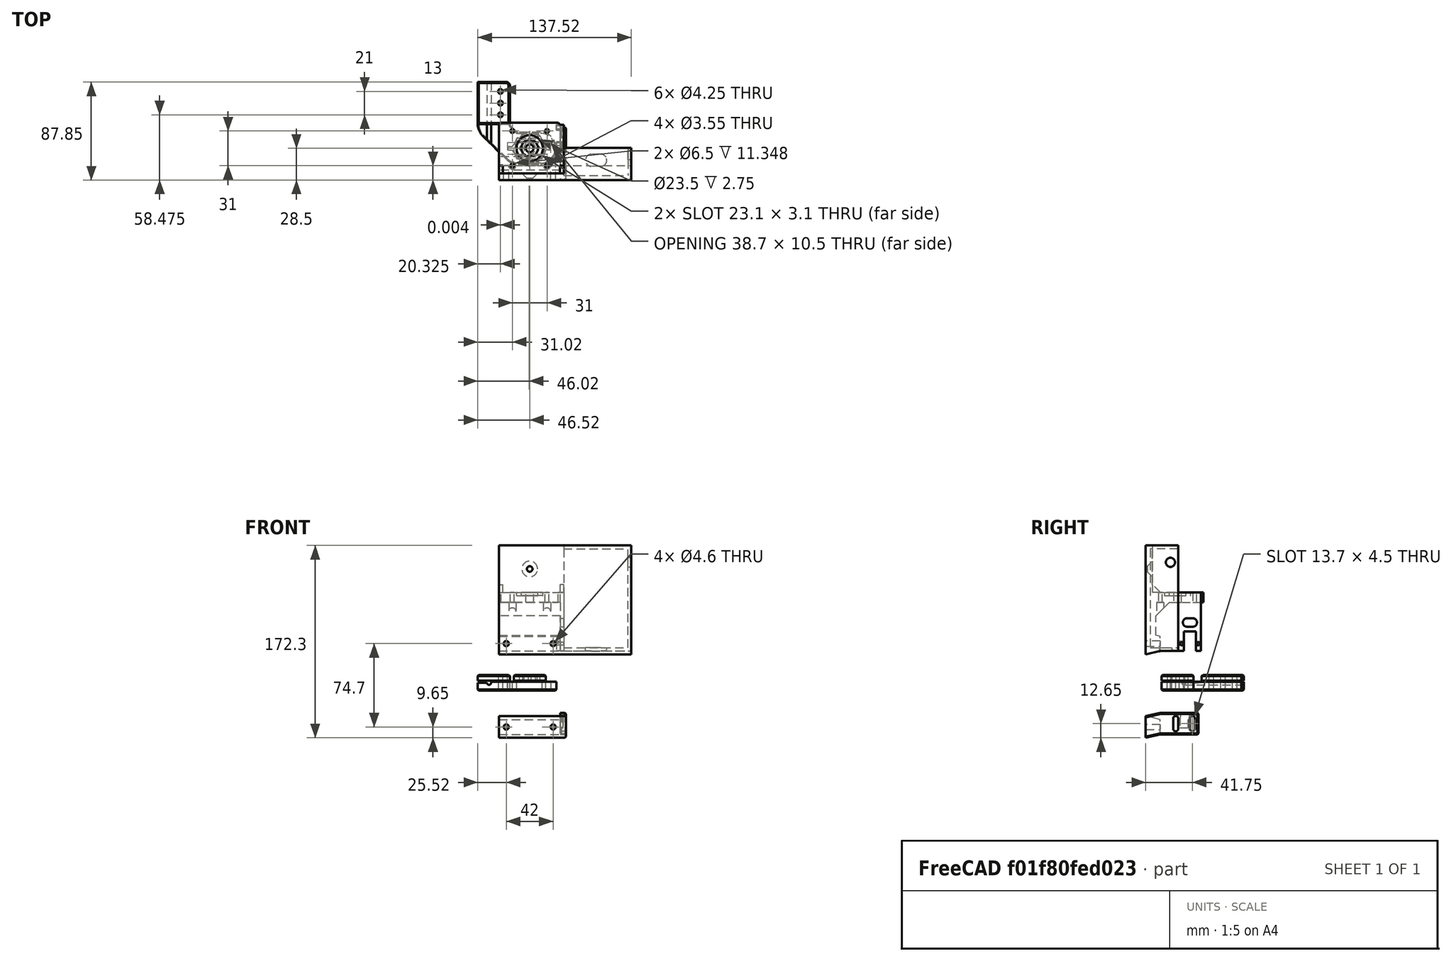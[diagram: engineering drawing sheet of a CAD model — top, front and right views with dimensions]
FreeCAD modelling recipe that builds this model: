
FCSTD DOCUMENT  (FreeCAD 1.0RUnknown)
Label: Mount_Mk2
License: All rights reserved
LicenseURL: https://en.wikipedia.org/wiki/All_rights_reserved
objects: Sketcher::SketchObject×24, PartDesign::Pad×13, PartDesign::Pocket×10, PartDesign::Chamfer×6, App::FeaturePython×6, PartDesign::Body×5, App::Link×5, Spreadsheet::Sheet×1, PartDesign::Hole×1, Assembly::JointGroup×1, Assembly::AssemblyObject×1
note: 143 computed .brp shape members not serialized (recipe doc carries the construction recipe); baked Part::Feature solids carry a one-line shape summary decoded from their .brp

FEATURE [Sketcher::SketchObject] Sketch
  ArcFitTolerance = 1e-06
  AttachmentSupport = -> [XZ_Plane]
  FullyConstrained = true
  MakeInternals = false
  MapMode = 5
  Placement = pos=(0,0,0) rot=(1,0,0;1.5708rad)
  sketch-geometry (6):
    g0: LineSegment StartX=0 StartY=0 StartZ=0 EndX=19.3 EndY=0 EndZ=0
    g1: LineSegment StartX=19.3 StartY=0 StartZ=0 EndX=16.3 EndY=13 EndZ=0
    g2: LineSegment StartX=16.3 StartY=13 StartZ=0 EndX=3 EndY=13 EndZ=0
    g3: LineSegment StartX=3 StartY=13 StartZ=0 EndX=0 EndY=0 EndZ=0
    g4: LineSegment [constr] StartX=16.3 StartY=13 StartZ=0 EndX=19.3 EndY=13 EndZ=0
    g5: LineSegment [constr] StartX=19.3 StartY=13 StartZ=0 EndX=19.3 EndY=0 EndZ=0
  constraints (16):
    c: Coincident(g-1,g0)
    c: PointOnObject(g0,g-1)
    c: Coincident(g0,g1)
    c: Coincident(g1,g2)
    c: Horizontal(g2)
    c: Coincident(g2,g3)
    c: Coincident(g3,g0)
    c: Equal(g3,g1)
    c: DistanceX(g2,g2) = 13.3
    c: Coincident(g1,g4)
    c: Horizontal(g4)
    c: Coincident(g4,g5)
    c: Coincident(g5,g0)
    c: Vertical(g5)
    c: DistanceY(g5,g5) = 13
    c: DistanceX(g4,g4) = 3
FEATURE [PartDesign::Pad] Pad
  Direction = (0,-1,2e-16)
  Length = 55
  Length2 = 10
  Placement = pos=(0,0,0) rot=(1,0,0;1.5708rad)
  Profile = -> Sketch
  ReferenceAxis = -> Sketch [N_Axis]
  Refine = true
  Suppressed = false
  Type = 0
FEATURE [Sketcher::SketchObject] Sketch001
  ArcFitTolerance = 1e-06
  AttachmentSupport = -> [Pad]
  ExternalGeometry = -> [Pad]
  FullyConstrained = true
  MakeInternals = false
  MapMode = 5
  Placement = pos=(0,5.7e-15,13) rot=(0,0,1;3.14159rad)
  sketch-geometry (5):
    g0: Circle CenterX=-9.65 CenterY=6.5 CenterZ=0 NormalX=0 NormalY=0 NormalZ=1 AngleXU=0 Radius=2.3
    g1: Circle CenterX=-9.65 CenterY=48.5 CenterZ=0 NormalX=0 NormalY=0 NormalZ=1 AngleXU=0 Radius=2.3
    g2: LineSegment [constr] StartX=-9.65 StartY=6.5 StartZ=0 EndX=-9.65 EndY=48.5 EndZ=0
    g3: LineSegment [constr] StartX=-9.65 StartY=48.5 StartZ=0 EndX=-9.65 EndY=55 EndZ=0
    g4: LineSegment [constr] StartX=-9.65 StartY=6.5 StartZ=0 EndX=-9.65 EndY=0 EndZ=0
  constraints (12):
    c: Coincident(g2,g0)
    c: Coincident(g2,g1)
    c: Vertical(g2)
    c: Coincident(g3,g1)
    c: Symmetric(g-6,g-6,g3)
    c: Vertical(g3)
    c: Coincident(g4,g0)
    c: Symmetric(g-5,g-5,g4)
    c: Equal(g0,g1)
    c: DistanceY(g2,g2) = 42
    c: Equal(g3,g4)
    c: Diameter(g1) = 4.6
FEATURE [PartDesign::Pocket] Pocket
  BaseFeature = -> Pad
  Direction = (0,0,-1)
  Length = 5
  Length2 = 5
  Placement = pos=(0,0,0) rot=(1,0,0;1.5708rad)
  Profile = -> Sketch001
  ReferenceAxis = -> Sketch001 [N_Axis]
  Refine = true
  Suppressed = false
  Type = 1
FEATURE [Sketcher::SketchObject] Sketch002
  ArcFitTolerance = 1e-06
  AttachmentSupport = -> [XZ_Plane001]
  FullyConstrained = true
  MakeInternals = false
  MapMode = 5
  Placement = pos=(0,0,0) rot=(1,0,0;1.5708rad)
  sketch-geometry (32):
    g0: LineSegment StartX=0 StartY=0 StartZ=0 EndX=97.6 EndY=0 EndZ=0
    g1: LineSegment StartX=97.6 StartY=0 StartZ=0 EndX=94.6 EndY=13 EndZ=0
    g2: LineSegment StartX=94.6 StartY=13 StartZ=0 EndX=81.3 EndY=13 EndZ=0
    g3: LineSegment StartX=81.3 StartY=13 StartZ=0 EndX=80.3769 EndY=9 EndZ=0
    g4: LineSegment StartX=80.3769 StartY=9 StartZ=0 EndX=51.1 EndY=9 EndZ=0
    g5: LineSegment StartX=51.1 StartY=9 StartZ=0 EndX=51.1 EndY=51.55 EndZ=0
    g6: LineSegment StartX=51.1 StartY=51.55 StartZ=0 EndX=42.1 EndY=51.55 EndZ=0
    g7: LineSegment StartX=42.1 StartY=51.55 StartZ=0 EndX=42.1 EndY=6 EndZ=0
    g8: LineSegment StartX=42.1 StartY=6 StartZ=0 EndX=0 EndY=6 EndZ=0
    g9: LineSegment StartX=0 StartY=6 StartZ=0 EndX=0 EndY=0 EndZ=0
    g10: LineSegment [constr] StartX=94.6 StartY=13 StartZ=0 EndX=97.6 EndY=13 EndZ=0
    g11: LineSegment [constr] StartX=97.6 StartY=13 StartZ=0 EndX=97.6 EndY=0 EndZ=0
    g12: LineSegment [constr] StartX=80.3769 StartY=9 StartZ=0 EndX=78.3 EndY=0 EndZ=0
    g13: LineSegment [constr] StartX=78.3 StartY=0 StartZ=0 EndX=78.3 EndY=13 EndZ=0
    g14: LineSegment [constr] StartX=78.3 StartY=13 StartZ=0 EndX=81.3 EndY=13 EndZ=0
    g15: LineSegment [constr] StartX=81.3 StartY=13 StartZ=0 EndX=81.3 EndY=0 EndZ=0
    g16: LineSegment [constr] StartX=3 StartY=49.55 StartZ=0 EndX=42.3 EndY=49.55 EndZ=0
    g17: LineSegment [constr] StartX=42.3 StartY=7.45 StartZ=0 EndX=3 EndY=7.45 EndZ=0
    g18: LineSegment [constr] StartX=3 StartY=7.45 StartZ=0 EndX=3 EndY=49.55 EndZ=0
    g19: LineSegment [constr] StartX=42.3 StartY=45.5 StartZ=0 EndX=59.3 EndY=45.5 EndZ=0
    g20: LineSegment [constr] StartX=59.3 StartY=45.5 StartZ=0 EndX=59.3 EndY=42.5 EndZ=0
    g21: LineSegment [constr] StartX=59.3 StartY=42.5 StartZ=0 EndX=42.3 EndY=42.5 EndZ=0
    g22: LineSegment [constr] StartX=42.3 StartY=14.5 StartZ=0 EndX=59.3 EndY=14.5 EndZ=0
    g23: LineSegment [constr] StartX=59.3 StartY=14.5 StartZ=0 EndX=59.3 EndY=11.5 EndZ=0
    g24: LineSegment [constr] StartX=59.3 StartY=11.5 StartZ=0 EndX=42.3 EndY=11.5 EndZ=0
    g25: LineSegment [constr] StartX=42.3 StartY=49.55 StartZ=0 EndX=42.3 EndY=45.5 EndZ=0
    g26: LineSegment [constr] StartX=42.3 StartY=45.5 StartZ=0 EndX=42.3 EndY=42.5 EndZ=0
    g27: LineSegment [constr] StartX=42.3 StartY=42.5 StartZ=0 EndX=42.3 EndY=14.5 EndZ=0
    g28: LineSegment [constr] StartX=42.3 StartY=14.5 StartZ=0 EndX=42.3 EndY=11.5 EndZ=0
    g29: LineSegment [constr] StartX=42.3 StartY=11.5 StartZ=0 EndX=42.3 EndY=7.45 EndZ=0
    g30: LineSegment [constr] StartX=42.3 StartY=13 StartZ=0 EndX=59.3 EndY=13 EndZ=0
    g31: LineSegment [constr] StartX=42.3 StartY=44 StartZ=0 EndX=59.3 EndY=44 EndZ=0
  constraints (89):
    c: Coincident(g-1,g0)
    c: PointOnObject(g0,g-1)
    c: Coincident(g0,g1)
    c: Coincident(g1,g2)
    c: Horizontal(g2)
    c: Coincident(g2,g3)
    c: Coincident(g3,g4)
    c: Horizontal(g4)
    c: Coincident(g4,g5)
    c: Vertical(g5)
    c: Coincident(g5,g6)
    c: Horizontal(g6)
    c: Coincident(g6,g7)
    c: Vertical(g7)
    c: Coincident(g7,g8)
    c: PointOnObject(g8,g-2)
    c: Horizontal(g8)
    c: Coincident(g8,g9)
    c: Coincident(g9,g0)
    c: Coincident(g1,g10)
    c: Horizontal(g10)
    c: Coincident(g10,g11)
    c: Coincident(g11,g0)
    c: Vertical(g11)
    c: DistanceX(g2,g2) = 13.3
    c: Coincident(g3,g12)
    c: PointOnObject(g12,g0)
    c: Coincident(g12,g13)
    c: Vertical(g13)
    c: Coincident(g13,g14)
    c: Coincident(g14,g2)
    c: Parallel(g12,g3)
    c: Horizontal(g14)
    c: Equal(g14,g10)
    c: DistanceY(g11,g11) = 13
    c: Distance(g10,g10) = 3
    c: Coincident(g2,g15)
    c: PointOnObject(g15,g0)
    c: Vertical(g15)
    c: DistanceX(g6,g6) = 9
    c: DistanceY(g9,g9) = 6
    c: Horizontal(g16)
    c: Horizontal(g17)
    c: Coincident(g17,g18)
    c: Coincident(g18,g16)
    c: Vertical(g18)
    c: Horizontal(g19)
    c: Coincident(g19,g20)
    c: Vertical(g20)
    c: Coincident(g20,g21)
    c: Horizontal(g21)
    c: Horizontal(g22)
    c: Coincident(g22,g23)
    c: Vertical(g23)
    c: Coincident(g23,g24)
    c: Horizontal(g24)
    c: Equal(g19,g22)
    c: Equal(g20,g23)
    c: Coincident(g16,g25)
    c: Coincident(g25,g19)
    c: Vertical(g25)
    c: Coincident(g25,g26)
    c: Coincident(g26,g21)
    c: Vertical(g26)
    c: Coincident(g26,g27)
    c: Coincident(g27,g22)
    c: Vertical(g27)
    c: Coincident(g27,g28)
    c: Coincident(g28,g24)
    c: Vertical(g28)
    c: Coincident(g28,g29)
    c: Coincident(g29,g17)
    c: Vertical(g29)
    c: Equal(g25,g29)
    c: Symmetric(g28,g28,g30)
    c: Symmetric(g23,g23,g30)
    c: Symmetric(g26,g26,g31)
    c: Symmetric(g20,g20,g31)
    c: Distance(g31,g30) = 31
    c: DistanceY(g18,g18) = 42.1
    c: Distance(g7,g25) = 0.2
    c: Distance(g8,g30) = 7
    c: Distance(g6,g16) = 2
    c: DistanceX(g16,g16) = 39.3
    c: Distance(g18,g9) = 3
    c: Distance(g4,g30) = 4
    c: DistanceX(g19,g19) = 17
    c: DistanceY(g20,g20) = 3
    c: Distance(g15,g27) = 39
FEATURE [PartDesign::Pad] Pad001
  Direction = (0,-1,2e-16)
  Length = 55
  Length2 = 10
  Placement = pos=(0,0,0) rot=(1,0,0;1.5708rad)
  Profile = -> Sketch002
  ReferenceAxis = -> Sketch002 [N_Axis]
  Refine = true
  Suppressed = false
  Type = 0
FEATURE [Sketcher::SketchObject] Sketch003
  ArcFitTolerance = 1e-06
  AttachmentSupport = -> [Pad001]
  ExternalGeometry = -> [Pad001]
  FullyConstrained = true
  MakeInternals = false
  MapMode = 5
  Placement = pos=(42.1,0,0) rot=(0.707107,0,-0.707107;3.14159rad)
  sketch-geometry (13):
    g0: Circle CenterX=-44 CenterY=12 CenterZ=0 NormalX=0 NormalY=0 NormalZ=1 AngleXU=0 Radius=1.775
    g1: Circle CenterX=-44 CenterY=43 CenterZ=0 NormalX=0 NormalY=0 NormalZ=1 AngleXU=0 Radius=1.775
    g2: Circle CenterX=-13 CenterY=12 CenterZ=0 NormalX=0 NormalY=0 NormalZ=1 AngleXU=0 Radius=1.775
    g3: Circle CenterX=-13 CenterY=43 CenterZ=0 NormalX=0 NormalY=0 NormalZ=1 AngleXU=0 Radius=1.775
    g4: Circle CenterX=-28.5 CenterY=27.5 CenterZ=0 NormalX=0 NormalY=0 NormalZ=1 AngleXU=0 Radius=3.5
    g5: LineSegment [constr] StartX=-44 StartY=12 StartZ=0 EndX=-44 EndY=43 EndZ=0
    g6: LineSegment [constr] StartX=-44 StartY=43 StartZ=0 EndX=-13 EndY=43 EndZ=0
    g7: LineSegment [constr] StartX=-13 StartY=43 StartZ=0 EndX=-13 EndY=12 EndZ=0
    g8: LineSegment [constr] StartX=-13 StartY=12 StartZ=0 EndX=-44 EndY=12 EndZ=0
    g9: LineSegment [constr] StartX=-44 StartY=27.5 StartZ=0 EndX=-28.5 EndY=27.5 EndZ=0
    g10: LineSegment [constr] StartX=-28.5 StartY=27.5 StartZ=0 EndX=-28.5 EndY=12 EndZ=0
    g11: LineSegment [constr] StartX=-13 StartY=12 StartZ=0 EndX=-13 EndY=-3.6e-15 EndZ=0
    g12: LineSegment [constr] StartX=-13 StartY=43 StartZ=0 EndX=-13 EndY=55 EndZ=0
  constraints (33):
    c: Coincident(g5,g0)
    c: Coincident(g5,g1)
    c: Vertical(g5)
    c: Coincident(g5,g6)
    c: Coincident(g6,g3)
    c: Horizontal(g6)
    c: Coincident(g6,g7)
    c: Coincident(g7,g2)
    c: Vertical(g7)
    c: Coincident(g7,g8)
    c: Coincident(g8,g5)
    c: Horizontal(g8)
    c: Symmetric(g5,g5,g9)
    c: Coincident(g9,g4)
    c: Horizontal(g9)
    c: Coincident(g9,g10)
    c: Symmetric(g8,g8,g10)
    c: Vertical(g10)
    c: Equal(g6,g5)
    c: DistanceX(g6,g6) = 31
    c: Distance(g-5,g7) = 7
    c: Coincident(g11,g2)
    c: PointOnObject(g11,g-6)
    c: Vertical(g11)
    c: Coincident(g12,g3)
    c: Vertical(g12)
    c: Equal(g11,g12)
    c: Equal(g1,g0)
    c: Equal(g0,g3)
    c: Equal(g3,g2)
    c: Diameter(g1) = 3.55
    c: Diameter(g4) = 7
    c: PointOnObject(g12,g-3)
FEATURE [PartDesign::Pocket] Pocket001
  BaseFeature = -> Pad001
  Direction = (1,0,2e-16)
  Length = 0
  Length2 = 5
  Placement = pos=(0,0,0) rot=(1,0,0;1.5708rad)
  Profile = -> Sketch003
  ReferenceAxis = -> Sketch003 [N_Axis]
  Refine = true
  Suppressed = false
  Type = 3
  UpToFace = -> Pad001 [Face6]
FEATURE [Sketcher::SketchObject] Sketch004
  ArcFitTolerance = 1e-06
  AttachmentSupport = -> [Pocket001]
  ExternalGeometry = -> [Pocket001]
  FullyConstrained = true
  MakeInternals = false
  MapMode = 5
  Placement = pos=(42.1,0,0) rot=(0.707107,0,-0.707107;3.14159rad)
  sketch-geometry (2):
    g0: Circle CenterX=-28.5 CenterY=27.5 CenterZ=0 NormalX=0 NormalY=0 NormalZ=1 AngleXU=0 Radius=11.75
    g1: Circle CenterX=-28.5 CenterY=27.5 CenterZ=0 NormalX=0 NormalY=0 NormalZ=1 AngleXU=0 Radius=7.5
  constraints (4):
    c: Coincident(g0,g-3)
    c: Diameter(g0) = 23.5
    c: Coincident(g1,g0)
    c: Diameter(g1) = 15
FEATURE [PartDesign::Pocket] Pocket002
  BaseFeature = -> Pocket001
  Direction = (1,0,2e-16)
  Length = 2.75
  Length2 = 5
  Placement = pos=(0,0,0) rot=(1,0,0;1.5708rad)
  Profile = -> Sketch004
  ReferenceAxis = -> Sketch004 [N_Axis]
  Refine = true
  Suppressed = false
  Type = 0
FEATURE [Sketcher::SketchObject] Sketch005
  ArcFitTolerance = 1e-06
  AttachmentSupport = -> [Pocket002]
  ExternalGeometry = -> [Pocket002]
  FullyConstrained = true
  MakeInternals = false
  MapMode = 5
  Placement = pos=(0,5.7e-15,13) rot=(0,0,1;3.14159rad)
  sketch-geometry (5):
    g0: Circle CenterX=-87.95 CenterY=48.5 CenterZ=0 NormalX=0 NormalY=0 NormalZ=1 AngleXU=0 Radius=2.3
    g1: Circle CenterX=-87.95 CenterY=6.5 CenterZ=0 NormalX=0 NormalY=0 NormalZ=1 AngleXU=0 Radius=2.3
    g2: LineSegment [constr] StartX=-87.95 StartY=48.5 StartZ=0 EndX=-87.95 EndY=6.5 EndZ=0
    g3: LineSegment [constr] StartX=-87.95 StartY=48.5 StartZ=0 EndX=-87.95 EndY=55 EndZ=0
    g4: LineSegment [constr] StartX=-87.95 StartY=6.5 StartZ=0 EndX=-87.95 EndY=0 EndZ=0
  constraints (12):
    c: Coincident(g2,g0)
    c: Coincident(g2,g1)
    c: Vertical(g2)
    c: Coincident(g3,g0)
    c: Symmetric(g-3,g-3,g3)
    c: Coincident(g4,g1)
    c: Symmetric(g-6,g-6,g4)
    c: Vertical(g4)
    c: Equal(g3,g4)
    c: DistanceY(g2,g2) = 42
    c: Diameter(g0) = 4.6
    c: Equal(g0,g1)
FEATURE [PartDesign::Pocket] Pocket003
  BaseFeature = -> Pocket002
  Direction = (0,0,-1)
  Length = 5
  Length2 = 5
  Placement = pos=(0,0,0) rot=(1,0,0;1.5708rad)
  Profile = -> Sketch005
  ReferenceAxis = -> Sketch005 [N_Axis]
  Refine = true
  Suppressed = false
  Type = 1
FEATURE [PartDesign::Chamfer] Chamfer
  Angle = 45
  Base = -> Pocket003 [Edge15,Edge23]
  BaseFeature = -> Pocket003
  ChamferType = 0
  FlipDirection = false
  Placement = pos=(0,0,0) rot=(1,0,0;1.5708rad)
  Refine = true
  Size = 2
  Size2 = 1
  SupportTransform = false
  Suppressed = false
  UseAllEdges = false
FEATURE [Sketcher::SketchObject] Sketch006
  ArcFitTolerance = 1e-06
  AttachmentSupport = -> [Chamfer]
  ExternalGeometry = -> [Chamfer]
  FullyConstrained = true
  MakeInternals = false
  MapMode = 5
  Placement = pos=(0,2.6e-15,6) rot=(0,0,1;3.14159rad)
  sketch-geometry (3):
    g0: Circle CenterX=-21.05 CenterY=27.5 CenterZ=0 NormalX=0 NormalY=0 NormalZ=1 AngleXU=0 Radius=2.5
    g1: LineSegment [constr] StartX=-21.05 StartY=27.5 StartZ=0 EndX=0 EndY=27.5 EndZ=0
    g2: LineSegment [constr] StartX=-21.05 StartY=27.5 StartZ=0 EndX=-21.05 EndY=55 EndZ=0
  constraints (7):
    c: Coincident(g1,g0)
    c: Symmetric(g-4,g-4,g1)
    c: Horizontal(g1)
    c: Coincident(g2,g0)
    c: Symmetric(g-3,g-3,g2)
    c: Vertical(g2)
    c: Diameter(g0) = 5
FEATURE [PartDesign::Pocket] Pocket004
  BaseFeature = -> Chamfer
  Direction = (0,0,-1)
  Length = 5
  Length2 = 5
  Placement = pos=(0,0,0) rot=(1,0,0;1.5708rad)
  Profile = -> Sketch006
  ReferenceAxis = -> Sketch006 [N_Axis]
  Refine = true
  Suppressed = false
  Type = 1
FEATURE [PartDesign::Chamfer] Chamfer001
  Angle = 45
  Base = -> Pocket004 [Edge38]
  BaseFeature = -> Pocket004
  ChamferType = 0
  FlipDirection = false
  Placement = pos=(0,0,0) rot=(1,0,0;1.5708rad)
  Refine = true
  Size = 4.5
  Size2 = 1
  SupportTransform = false
  Suppressed = false
  UseAllEdges = false
FEATURE [Sketcher::SketchObject] Sketch007
  ArcFitTolerance = 1e-06
  AttachmentSupport = -> [XY_Plane002]
  FullyConstrained = true
  MakeInternals = false
  MapMode = 5
  expr: Constraints[122] = 3.9 + 0.35
  expr: Constraints[72] = (2.9 + 0.2) / 2
  expr: Constraints[73] = (10 + 0.5) / 2
  sketch-geometry (53):
    g0: ArcOfCircle CenterX=0 CenterY=0 CenterZ=0 NormalX=0 NormalY=0 NormalZ=1 AngleXU=0 Radius=14.35 StartAngle=4.71239 EndAngle=7.85398
    g1: ArcOfCircle CenterX=-20 CenterY=9e-16 CenterZ=0 NormalX=0 NormalY=0 NormalZ=1 AngleXU=0 Radius=14.35 StartAngle=3.92699 EndAngle=4.71239
    g2: ArcOfCircle CenterX=-41.666 CenterY=21.666 CenterZ=0 NormalX=0 NormalY=0 NormalZ=1 AngleXU=0 Radius=14.35 StartAngle=3.14159 EndAngle=3.92699
    g3: ArcOfCircle CenterX=0 CenterY=7.8 CenterZ=0 NormalX=0 NormalY=0 NormalZ=1 AngleXU=0 Radius=1.55 StartAngle=4.71239 EndAngle=7.85398
    g4: ArcOfCircle CenterX=-20 CenterY=7.8 CenterZ=0 NormalX=0 NormalY=0 NormalZ=1 AngleXU=0 Radius=1.55 StartAngle=1.5708 EndAngle=4.71239
    g5: ArcOfCircle CenterX=-20 CenterY=-7.8 CenterZ=0 NormalX=0 NormalY=0 NormalZ=1 AngleXU=0 Radius=1.55 StartAngle=1.5708 EndAngle=4.71239
    g6: ArcOfCircle CenterX=0 CenterY=-7.8 CenterZ=0 NormalX=0 NormalY=0 NormalZ=1 AngleXU=0 Radius=1.55 StartAngle=4.71239 EndAngle=7.85398
    g7: ArcOfCircle CenterX=7.8 CenterY=-3e-16 CenterZ=0 NormalX=0 NormalY=0 NormalZ=1 AngleXU=0 Radius=1.55 StartAngle=4.71239 EndAngle=7.85398
    g8: ArcOfCircle CenterX=-27.8 CenterY=1.7e-15 CenterZ=0 NormalX=0 NormalY=0 NormalZ=1 AngleXU=0 Radius=1.55 StartAngle=1.5708 EndAngle=4.71239
    g9: LineSegment StartX=-20 StartY=9.35 StartZ=0 EndX=0 EndY=9.35 EndZ=0
    g10: LineSegment StartX=-20 StartY=6.25 StartZ=0 EndX=0 EndY=6.25 EndZ=0
    g11: LineSegment StartX=-20 StartY=5.25 StartZ=0 EndX=0 EndY=5.25 EndZ=0
    g12: LineSegment StartX=-20 StartY=-5.25 StartZ=0 EndX=0 EndY=-5.25 EndZ=0
    g13: LineSegment StartX=-20 StartY=-6.25 StartZ=0 EndX=0 EndY=-6.25 EndZ=0
    g14: LineSegment StartX=-20 StartY=-9.35 StartZ=0 EndX=0 EndY=-9.35 EndZ=0
    g15: LineSegment StartX=-20 StartY=-14.35 StartZ=0 EndX=-3.6e-15 EndY=-14.35 EndZ=0
    g16: LineSegment StartX=-27.8 StartY=1.55 StartZ=0 EndX=-25.016 EndY=1.55 EndZ=0
    g17: LineSegment StartX=-27.8 StartY=-1.55 StartZ=0 EndX=-25.016 EndY=-1.55 EndZ=0
    g18: LineSegment StartX=5.01597 StartY=1.55 StartZ=0 EndX=7.8 EndY=1.55 EndZ=0
    g19: LineSegment StartX=7.8 StartY=-1.55 StartZ=0 EndX=5.01597 EndY=-1.55 EndZ=0
    g20: LineSegment StartX=4.4e-15 StartY=14.35 StartZ=0 EndX=-20 EndY=14.35 EndZ=0
    g21: LineSegment StartX=-51.813 StartY=11.519 StartZ=0 EndX=-30.147 EndY=-10.147 EndZ=0
    g22: LineSegment StartX=-56.016 StartY=21.666 StartZ=0 EndX=-56.016 EndY=59.35 EndZ=0
    g23: LineSegment [constr] StartX=-20 StartY=-1e-16 StartZ=0 EndX=-20 EndY=7.8 EndZ=0
    g24: LineSegment [constr] StartX=-20 StartY=-7.8 StartZ=0 EndX=-20 EndY=0 EndZ=0
    g25: LineSegment [constr] StartX=0 StartY=-7.8 StartZ=0 EndX=0 EndY=0 EndZ=0
    g26: LineSegment [constr] StartX=0 StartY=0 StartZ=0 EndX=0 EndY=7.8 EndZ=0
    g27: LineSegment [constr] StartX=0 StartY=0 StartZ=0 EndX=7.8 EndY=-3e-16 EndZ=0
    g28: LineSegment [constr] StartX=-27.8 StartY=1.7e-15 StartZ=0 EndX=-20 EndY=-1e-16 EndZ=0
    g29: ArcOfCircle CenterX=0 CenterY=0 CenterZ=0 NormalX=0 NormalY=0 NormalZ=1 AngleXU=0 Radius=5.25 StartAngle=0.299705 EndAngle=1.5708
    g30: ArcOfCircle CenterX=0 CenterY=0 CenterZ=0 NormalX=0 NormalY=0 NormalZ=1 AngleXU=0 Radius=5.25 StartAngle=4.71239 EndAngle=5.98348
    g31: ArcOfCircle CenterX=-20 CenterY=-1e-16 CenterZ=0 NormalX=0 NormalY=0 NormalZ=1 AngleXU=0 Radius=5.25 StartAngle=1.5708 EndAngle=2.84189
    g32: ArcOfCircle CenterX=-20 CenterY=-1e-16 CenterZ=0 NormalX=0 NormalY=0 NormalZ=1 AngleXU=0 Radius=5.25 StartAngle=3.4413 EndAngle=4.71239
    g33: LineSegment StartX=-21.4142 StartY=14.9358 StartZ=0 EndX=-26.7302 EndY=20.2518 EndZ=0
    g34: LineSegment StartX=-27.316 StartY=21.666 StartZ=0 EndX=-27.316 EndY=57.2287 EndZ=0
    g35: ArcOfCircle CenterX=-25.316 CenterY=21.666 CenterZ=0 NormalX=0 NormalY=0 NormalZ=1 AngleXU=0 Radius=2 StartAngle=3.14159 EndAngle=3.92699
    g36: ArcOfCircle CenterX=-20 CenterY=16.35 CenterZ=0 NormalX=0 NormalY=0 NormalZ=1 AngleXU=0 Radius=2 StartAngle=3.92699 EndAngle=4.71239
    g37: LineSegment StartX=-27.316 StartY=57.2287 StartZ=0 EndX=-29.4373 EndY=59.35 EndZ=0
    g38: LineSegment StartX=-56.016 StartY=59.35 StartZ=0 EndX=-29.4373 EndY=59.35 EndZ=0
    g39: LineSegment [constr] StartX=-20 StartY=-14.35 StartZ=0 EndX=-56.016 EndY=-14.35 EndZ=0
    g40: LineSegment [constr] StartX=-56.016 StartY=-14.35 StartZ=0 EndX=-56.016 EndY=21.666 EndZ=0
    g41: LineSegment [constr] StartX=-47.766 StartY=59.35 StartZ=0 EndX=-47.766 EndY=-14.35 EndZ=0
    g42: LineSegment [constr] StartX=-44.016 StartY=59.35 StartZ=0 EndX=-44.016 EndY=-14.35 EndZ=0
    g43: Circle CenterX=-35.691 CenterY=50.975 CenterZ=0 NormalX=0 NormalY=0 NormalZ=1 AngleXU=0 Radius=2.125
    g44: Circle CenterX=-35.691 CenterY=40.475 CenterZ=0 NormalX=0 NormalY=0 NormalZ=1 AngleXU=0 Radius=2.125
    g45: Circle CenterX=-35.691 CenterY=29.975 CenterZ=0 NormalX=0 NormalY=0 NormalZ=1 AngleXU=0 Radius=2.125
    g46: LineSegment [constr] StartX=-35.691 StartY=53.1 StartZ=0 EndX=-35.691 EndY=59.35 EndZ=0
    g47: LineSegment [constr] StartX=-35.691 StartY=48.85 StartZ=0 EndX=-35.691 EndY=42.6 EndZ=0
    g48: LineSegment [constr] StartX=-35.691 StartY=38.35 StartZ=0 EndX=-35.691 EndY=32.1 EndZ=0
    g49: LineSegment [constr] StartX=-56.016 StartY=21.666 StartZ=0 EndX=-27.316 EndY=21.666 EndZ=0
    g50: LineSegment [constr] StartX=-33.566 StartY=50.975 StartZ=0 EndX=-27.316 EndY=50.975 EndZ=0
    g51: LineSegment [constr] StartX=-20 StartY=7.8 StartZ=0 EndX=-20 EndY=14.35 EndZ=0
    g52: LineSegment [constr] StartX=-20 StartY=-7.8 StartZ=0 EndX=-20 EndY=-14.35 EndZ=0
  constraints (142):
    c: Horizontal(g9)
    c: Horizontal(g10)
    c: Horizontal(g11)
    c: Horizontal(g12)
    c: Horizontal(g13)
    c: Horizontal(g14)
    c: Horizontal(g15)
    c: Tangent(g9,g4) = 1.5708
    c: Tangent(g10,g4) = -1.5708
    c: Tangent(g10,g3) = -1.5708
    c: Tangent(g9,g3) = 1.5708
    c: Tangent(g13,g6) = 1.5708
    c: Tangent(g14,g6) = -1.5708
    c: Tangent(g13,g5) = 1.5708
    c: Tangent(g14,g5) = -1.5708
    c: Horizontal(g16)
    c: Horizontal(g18)
    c: Horizontal(g19)
    c: Horizontal(g17)
    c: Tangent(g16,g8) = 1.5708
    c: Tangent(g17,g8) = -1.5708
    c: Equal(g16,g17)
    c: Tangent(g18,g7) = 1.5708
    c: Tangent(g19,g7) = 1.5708
    c: Equal(g18,g19)
    c: Horizontal(g20)
    c: Tangent(g21,g1) = -1.5708
    c: Tangent(g21,g2) = -1.5708
    c: Angle(g15,g21) = 2.35619
    c: Vertical(g22)
    c: Tangent(g22,g2) = 1.5708
    c: Tangent(g15,g0) = -1.5708
    c: Tangent(g20,g0) = -1.5708
    c: Tangent(g15,g1) = -1.5708
    c: Coincident(g0,g-1)
    c: Coincident(g23,g4)
    c: Vertical(g23)
    c: Coincident(g24,g5)
    c: Coincident(g25,g6)
    c: Coincident(g25,g0)
    c: Coincident(g26,g0)
    c: Coincident(g26,g3)
    c: Vertical(g24)
    c: Vertical(g25)
    c: Vertical(g26)
    c: Equal(g23,g24)
    c: Coincident(g27,g0)
    c: Coincident(g27,g7)
    c: Coincident(g28,g8)
    c: Coincident(g29,g0)
    c: Coincident(g29,g18)
    c: Coincident(g30,g0)
    c: Coincident(g30,g19)
    c: Coincident(g31,g23)
    c: Coincident(g31,g16)
    c: Coincident(g32,g24)
    c: Coincident(g32,g17)
    c: Equal(g30,g29)
    c: Equal(g29,g32)
    c: Coincident(g24,g23)
    c: Coincident(g24,g28)
    c: Equal(g27,g26)
    c: Equal(g23,g28)
    c: Equal(g8,g4)
    c: Equal(g5,g4)
    c: Tangent(g31,g11) = 1.5708
    c: Tangent(g32,g12) = -1.5708
    c: Tangent(g29,g11) = 1.5708
    c: Tangent(g30,g12) = -1.5708
    c: Equal(g7,g8)
    c: DistanceX(g11,g11) = 20
    c: DistanceY(g26,g26) = 7.8
    c: Radius(g3) = 1.55
    c: Radius(g31) = 5.25
    c: Distance(g20,g9) = 5
    c: Vertical(g34)
    c: Equal(g35,g36)
    c: Equal(g2,g1)
    c: Equal(g1,g0)
    c: Radius(g36) = 2
    c: Tangent(g36,g20) = 1.5708
    c: Tangent(g36,g33) = 1.5708
    c: Tangent(g35,g33) = 1.5708
    c: Tangent(g35,g34) = 1.5708
    c: Parallel(g21,g33)
    c: Coincident(g37,g34)
    c: Coincident(g38,g22)
    c: Coincident(g38,g37)
    c: Horizontal(g38)
    c: Angle(g38,g37) = 2.35619
    c: Distance(g37,g37) = 3
    c: Tangent(g39,g1) = 1.5708
    c: Vertical(g40)
    c: Coincident(g2,g40)
    c: Coincident(g40,g39)
    c: PointOnObject(g41,g38)
    c: PointOnObject(g41,g39)
    c: Vertical(g41)
    c: PointOnObject(g42,g38)
    c: PointOnObject(g42,g39)
    c: Vertical(g42)
    c: Distance(g42,g22) = 12
    c: Distance(g42,g41) = 3.75
    c: Distance(g16,g42) = 19
    c: Distance(g20,g38) = 45
    c: Equal(g43,g44)
    c: Equal(g44,g45)
    c: PointOnObject(g46,g43)
    c: PointOnObject(g46,g38)
    c: Vertical(g46)
    c: PointOnObject(g47,g43)
    c: PointOnObject(g47,g44)
    c: Vertical(g47)
    c: PointOnObject(g48,g44)
    c: PointOnObject(g48,g45)
    c: Vertical(g48)
    c: Perpendicular(g43,g46)
    c: Perpendicular(g43,g47)
    c: Perpendicular(g44,g47)
    c: Perpendicular(g44,g48)
    c: Perpendicular(g45,g48)
    c: Equal(g47,g48)
    c: Diameter(g45) = 4.25
    c: Coincident(g49,g2)
    c: Coincident(g49,g34)
    c: Horizontal(g49)
    c: PointOnObject(g50,g43)
    c: PointOnObject(g50,g34)
    c: Horizontal(g50)
    c: Perpendicular(g43,g50)
    c: DistanceX(g50,g50) = 6.25
    c: Coincident(g51,g4)
    c: Coincident(g51,g20)
    c: Coincident(g52,g5)
    c: Coincident(g52,g1)
    c: Vertical(g52)
    c: Vertical(g51)
    c: Equal(g46,g47)
    c: Equal(g50,g46)
    c: Distance(g34,g22) = 28.7
    c: DistanceY(g22,g22) = 37.684
    c: Distance(g0,g38) = 59.35
FEATURE [Spreadsheet::Sheet] Spreadsheet  label="Params"
  cells = A2='M3 Shaft Diameter; B2==2.9 mm; A3='M4 Shaft Diameter; B3==3.9 mm; A4='Bolt Tolerance; B4==0.2 mm; A6='Part Thickness; B6==8 mm; A8='Main Slot Length; B8==20 mm; A9='Main Slot Diameter; B9==10 mm; A10='Main Slot Tolerance; B10==0.5 mm; A11='Object Diameter; B11==28 mm; A13='Window Grab Diameter; B13==3.75 mm; A14='Window Grab Length; B14==12 mm; A15='Window Grab Thickness; B15==2 mm
FEATURE [PartDesign::Pad] Pad002
  Direction = (0,0,1)
  Length = 8
  Length2 = 10
  Profile = -> Sketch007
  ReferenceAxis = -> Sketch007 [N_Axis]
  Refine = true
  Suppressed = false
  Type = 0
FEATURE [Sketcher::SketchObject] Sketch008
  ArcFitTolerance = 1e-06
  AttachmentSupport = -> [Pad002]
  ExternalGeometry = -> [Pad002]
  FullyConstrained = true
  MakeInternals = false
  MapMode = 5
  Placement = pos=(0,59.35,0) rot=(0,0.707107,0.707107;3.14159rad)
  expr: Constraints[12] = 3.75 / 2
  sketch-geometry (5):
    g0: LineSegment StartX=56.016 StartY=7 StartZ=0 EndX=47.766 EndY=7 EndZ=0
    g1: LineSegment StartX=44.016 StartY=8 StartZ=0 EndX=44.016 EndY=7 EndZ=0
    g2: ArcOfCircle CenterX=45.891 CenterY=7 CenterZ=0 NormalX=0 NormalY=0 NormalZ=1 AngleXU=0 Radius=1.875 StartAngle=3.14159 EndAngle=6.28319
    g3: LineSegment StartX=44.016 StartY=8 StartZ=0 EndX=56.016 EndY=8 EndZ=0
    g4: LineSegment StartX=56.016 StartY=8 StartZ=0 EndX=56.016 EndY=7 EndZ=0
  constraints (14):
    c: PointOnObject(g0,g-4)
    c: Horizontal(g0)
    c: PointOnObject(g1,g-3)
    c: Vertical(g1)
    c: Coincident(g2,g0)
    c: Tangent(g2,g1) = -1.5708
    c: Perpendicular(g2,g0)
    c: Coincident(g3,g1)
    c: Coincident(g3,g-4)
    c: Coincident(g4,g3)
    c: Coincident(g4,g0)
    c: DistanceX(g3,g3) = 12
    c: Radius(g2) = 1.875
    c: DistanceY(g4,g4) = 1
FEATURE [PartDesign::Pocket] Pocket005
  BaseFeature = -> Pad002
  Direction = (0,-1,2e-16)
  Length = 5
  Length2 = 5
  Profile = -> Sketch008
  ReferenceAxis = -> Sketch008 [N_Axis]
  Refine = true
  Suppressed = false
  Type = 1
FEATURE [Sketcher::SketchObject] Sketch009
  ArcFitTolerance = 1e-06
  AttachmentSupport = -> [XY_Plane003]
  FullyConstrained = true
  MakeInternals = false
  MapMode = 5
  expr: Constraints[16] = 3.9 + 0.35
  sketch-geometry (12):
    g0: LineSegment StartX=0 StartY=-2.12132 StartZ=0 EndX=-2.12132 EndY=0 EndZ=0
    g1: LineSegment StartX=-2.12132 StartY=0 StartZ=0 EndX=-28.7 EndY=0 EndZ=0
    g2: LineSegment StartX=-28.7 StartY=0 StartZ=0 EndX=-28.7 EndY=-37.684 EndZ=0
    g3: LineSegment StartX=-28.7 StartY=-37.684 StartZ=0 EndX=0 EndY=-37.684 EndZ=0
    g4: LineSegment StartX=0 StartY=-37.684 StartZ=0 EndX=0 EndY=-2.12132 EndZ=0
    g5: Circle CenterX=-8.375 CenterY=-8.375 CenterZ=0 NormalX=0 NormalY=0 NormalZ=1 AngleXU=0 Radius=2.125
    g6: Circle CenterX=-8.375 CenterY=-18.875 CenterZ=0 NormalX=0 NormalY=0 NormalZ=1 AngleXU=0 Radius=2.125
    g7: Circle CenterX=-8.375 CenterY=-29.375 CenterZ=0 NormalX=0 NormalY=0 NormalZ=1 AngleXU=0 Radius=2.125
    g8: LineSegment [constr] StartX=-8.375 StartY=0 StartZ=0 EndX=-8.375 EndY=-6.25 EndZ=0
    g9: LineSegment [constr] StartX=-6.25 StartY=-8.375 StartZ=0 EndX=0 EndY=-8.375 EndZ=0
    g10: LineSegment [constr] StartX=-8.375 StartY=-16.75 StartZ=0 EndX=-8.375 EndY=-10.5 EndZ=0
    g11: LineSegment [constr] StartX=-8.375 StartY=-27.25 StartZ=0 EndX=-8.375 EndY=-21 EndZ=0
  constraints (40):
    c: PointOnObject(g0,g-2)
    c: PointOnObject(g0,g-1)
    c: Coincident(g0,g1)
    c: PointOnObject(g1,g-1)
    c: Coincident(g1,g2)
    c: Vertical(g2)
    c: Coincident(g2,g3)
    c: PointOnObject(g3,g-2)
    c: Horizontal(g3)
    c: Coincident(g3,g4)
    c: Coincident(g4,g0)
    c: Distance(g0,g0) = 3
    c: Angle(g1,g0) = 2.35619
    c: DistanceY(g2,g2) = 37.684
    c: Equal(g6,g5)
    c: Equal(g5,g7)
    c: Diameter(g7) = 4.25
    c: PointOnObject(g8,g1)
    c: PointOnObject(g8,g5)
    c: Vertical(g8)
    c: PointOnObject(g9,g5)
    c: PointOnObject(g9,g4)
    c: PointOnObject(g10,g6)
    c: PointOnObject(g10,g5)
    c: Vertical(g10)
    c: PointOnObject(g11,g7)
    c: PointOnObject(g11,g6)
    c: Vertical(g11)
    c: Horizontal(g9)
    c: Perpendicular(g5,g8)
    c: Perpendicular(g5,g9)
    c: Perpendicular(g5,g10)
    c: Perpendicular(g6,g10)
    c: Perpendicular(g6,g11)
    c: Perpendicular(g7,g11)
    c: Equal(g9,g8)
    c: Equal(g8,g10)
    c: Equal(g10,g11)
    c: DistanceX(g9,g9) = 6.25
    c: Distance(g4,g2) = 28.7
FEATURE [PartDesign::Pad] Pad003
  Direction = (0,0,1)
  Length = 5
  Length2 = 10
  Profile = -> Sketch009
  ReferenceAxis = -> Sketch009 [N_Axis]
  Refine = true
  Suppressed = false
  Type = 0
FEATURE [Sketcher::SketchObject] Sketch010
  ArcFitTolerance = 1e-06
  AttachmentSupport = -> [XY_Plane004]
  FullyConstrained = true
  MakeInternals = false
  MapMode = 5
  expr: Constraints[20] = 10 + 0.5
  sketch-geometry (11):
    g0: Circle CenterX=0 CenterY=0 CenterZ=0 NormalX=0 NormalY=0 NormalZ=1 AngleXU=0 Radius=14.35
    g1: Circle CenterX=0 CenterY=0 CenterZ=0 NormalX=0 NormalY=0 NormalZ=1 AngleXU=0 Radius=5.25
    g2: Circle CenterX=0 CenterY=7.8 CenterZ=0 NormalX=0 NormalY=0 NormalZ=1 AngleXU=0 Radius=1.5
    g3: Circle CenterX=7.8 CenterY=0 CenterZ=0 NormalX=0 NormalY=0 NormalZ=1 AngleXU=0 Radius=1.5
    g4: Circle CenterX=-7.8 CenterY=0 CenterZ=0 NormalX=0 NormalY=0 NormalZ=1 AngleXU=0 Radius=1.5
    g5: Circle CenterX=0 CenterY=-7.8 CenterZ=0 NormalX=0 NormalY=0 NormalZ=1 AngleXU=0 Radius=1.5
    g6: LineSegment [constr] StartX=0 StartY=0 StartZ=0 EndX=0 EndY=7.8 EndZ=0
    g7: LineSegment [constr] StartX=0 StartY=0 StartZ=0 EndX=-7.8 EndY=0 EndZ=0
    g8: LineSegment [constr] StartX=0 StartY=0 StartZ=0 EndX=0 EndY=-7.8 EndZ=0
    g9: LineSegment [constr] StartX=0 StartY=0 StartZ=0 EndX=7.8 EndY=0 EndZ=0
    g10: LineSegment [constr] StartX=0 StartY=7.8 StartZ=0 EndX=0 EndY=14.35 EndZ=0
  constraints (27):
    c: Coincident(g0,g-1)
    c: Coincident(g1,g0)
    c: PointOnObject(g2,g-2)
    c: PointOnObject(g3,g-1)
    c: PointOnObject(g4,g-1)
    c: PointOnObject(g5,g-2)
    c: Coincident(g6,g0)
    c: Coincident(g6,g2)
    c: Coincident(g7,g0)
    c: Coincident(g7,g4)
    c: Coincident(g8,g0)
    c: Coincident(g8,g5)
    c: Coincident(g9,g0)
    c: Coincident(g9,g3)
    c: Equal(g6,g7)
    c: Equal(g7,g9)
    c: Equal(g9,g8)
    c: Equal(g2,g4)
    c: Equal(g4,g5)
    c: Equal(g5,g3)
    c: Diameter(g1) = 10.5
    c: Diameter(g3) = 3
    c: DistanceY(g6,g6) = 7.8
    c: Coincident(g10,g2)
    c: PointOnObject(g10,g0)
    c: Vertical(g10)
    c: DistanceY(g10,g10) = 6.55
FEATURE [PartDesign::Pad] Pad004
  Direction = (0,0,1)
  Length = 5
  Length2 = 10
  Profile = -> Sketch010
  ReferenceAxis = -> Sketch010 [N_Axis]
  Refine = true
  Suppressed = false
  Type = 0
FEATURE [PartDesign::Chamfer] Chamfer002
  Angle = 45
  Base = -> Pad004 [Edge3]
  BaseFeature = -> Pad004
  ChamferType = 0
  FlipDirection = false
  Refine = true
  Size = 1
  Size2 = 1
  SupportTransform = false
  Suppressed = false
  UseAllEdges = false
FEATURE [PartDesign::Body] Body004  label="Window_Grab_Arm_Clamp"
  AllowCompound = false
  Group = -> [Sketch010,Pad004,Chamfer002]
  Origin = -> Origin004
  Placement = pos=(1.5,3.5,9) rot=(0,0,1;0rad)
  Tip = -> Chamfer002
FEATURE [PartDesign::Chamfer] Chamfer003
  Angle = 45
  Base = -> Pocket005 [Edge15,Edge16,Edge1,Edge5,Edge6,Edge7,Edge8,Edge9,Edge10,Edge11,Edge12,Edge13,Edge14]
  BaseFeature = -> Pocket005
  ChamferType = 0
  FlipDirection = false
  Refine = true
  Size = 1
  Size2 = 1
  SupportTransform = false
  Suppressed = false
  UseAllEdges = false
FEATURE [PartDesign::Body] Body002  label="Window_Grab_Arm"
  AllowCompound = false
  Group = -> [Sketch007,Pad002,Sketch008,Pocket005,Chamfer003]
  Origin = -> Origin002
  Placement = pos=(11,3.5,0) rot=(0,0,1;0rad)
  Tip = -> Chamfer003
FEATURE [PartDesign::Chamfer] Chamfer004
  Angle = 45
  Base = -> Pad003 [Edge10,Edge7,Edge4,Edge15,Edge13]
  BaseFeature = -> Pad003
  ChamferType = 0
  FlipDirection = false
  Refine = true
  Size = 1
  Size2 = 1
  SupportTransform = false
  Suppressed = false
  UseAllEdges = false
FEATURE [PartDesign::Body] Body003  label="Window_Grab_Clamp"
  AllowCompound = false
  Group = -> [Sketch009,Pad003,Chamfer004]
  Origin = -> Origin003
  Placement = pos=(-16.32,62.85,9) rot=(0,0,1;0rad)
  Tip = -> Chamfer004
FEATURE [Sketcher::SketchObject] Sketch011
  ArcFitTolerance = 1e-06
  AttachmentSupport = -> [Chamfer001]
  ExternalGeometry = -> [Chamfer001]
  FullyConstrained = true
  MakeInternals = false
  MapMode = 5
  Placement = pos=(0,-55,1.21e-14) rot=(1,0,0;1.5708rad)
  sketch-geometry (8):
    g0: LineSegment StartX=42.1 StartY=49.55 StartZ=0 EndX=51.1 EndY=49.55 EndZ=0
    g1: LineSegment StartX=94.6 StartY=13 StartZ=0 EndX=97.6 EndY=0 EndZ=0
    g2: LineSegment StartX=97.6 StartY=0 StartZ=0 EndX=0 EndY=0 EndZ=0
    g3: LineSegment StartX=0 StartY=0 StartZ=0 EndX=0 EndY=6 EndZ=0
    g4: LineSegment StartX=0 StartY=6 StartZ=0 EndX=42.1 EndY=6 EndZ=0
    g5: LineSegment StartX=42.1 StartY=6 StartZ=0 EndX=42.1 EndY=49.55 EndZ=0
    g6: LineSegment StartX=51.1 StartY=49.55 StartZ=0 EndX=94.6 EndY=49.55 EndZ=0
    g7: LineSegment StartX=94.6 StartY=49.55 StartZ=0 EndX=94.6 EndY=13 EndZ=0
  constraints (17):
    c: Coincident(g-12,g0)
    c: Coincident(g0,g-12)
    c: Coincident(g1,g-9)
    c: Coincident(g1,g2)
    c: Coincident(g2,g-1)
    c: Coincident(g2,g3)
    c: Coincident(g3,g-4)
    c: Coincident(g3,g4)
    c: Coincident(g4,g-6)
    c: Coincident(g4,g5)
    c: Coincident(g5,g0)
    c: Coincident(g0,g6)
    c: Horizontal(g6)
    c: Coincident(g6,g7)
    c: Coincident(g7,g1)
    c: Vertical(g7)
    c: Coincident(g-10,g1)
FEATURE [PartDesign::Pad] Pad005
  BaseFeature = -> Chamfer001
  Direction = (0,-1,2e-16)
  Length = 3
  Length2 = 10
  Placement = pos=(0,0,0) rot=(1,0,0;1.5708rad)
  Profile = -> Sketch011
  ReferenceAxis = -> Sketch011 [N_Axis]
  Refine = true
  Suppressed = false
  Type = 0
FEATURE [Sketcher::SketchObject] Sketch012
  ArcFitTolerance = 1e-06
  AttachmentSupport = -> [Pad005]
  ExternalGeometry = -> [Pad005]
  FullyConstrained = true
  MakeInternals = false
  MapMode = 5
  Placement = pos=(0,-58,1.74e-14) rot=(1,0,0;1.5708rad)
  sketch-geometry (11):
    g0: LineSegment StartX=97.6 StartY=-5.3e-15 StartZ=0 EndX=0 EndY=0 EndZ=0
    g1: LineSegment StartX=0 StartY=0 StartZ=0 EndX=5e-16 EndY=4 EndZ=0
    g2: LineSegment [constr] StartX=5e-16 StartY=4 StartZ=0 EndX=96.6769 EndY=4 EndZ=0
    g3: LineSegment StartX=5e-16 StartY=4 StartZ=0 EndX=0 EndY=29 EndZ=0
    g4: LineSegment StartX=0 StartY=29 StartZ=0 EndX=3 EndY=29 EndZ=0
    g5: LineSegment StartX=3 StartY=29 StartZ=0 EndX=3 EndY=4 EndZ=0
    g6: LineSegment StartX=3 StartY=4 StartZ=0 EndX=91.6 EndY=4 EndZ=0
    g7: LineSegment StartX=91.6 StartY=4 StartZ=0 EndX=91.6 EndY=29 EndZ=0
    g8: LineSegment StartX=91.6 StartY=29 StartZ=0 EndX=94.6 EndY=29 EndZ=0
    g9: LineSegment StartX=97.6 StartY=-5.3e-15 StartZ=0 EndX=94.6 EndY=13 EndZ=0
    g10: LineSegment StartX=94.6 StartY=13 StartZ=0 EndX=94.6 EndY=29 EndZ=0
  constraints (31):
    c: Coincident(g0,g-1)
    c: Coincident(g0,g1)
    c: PointOnObject(g1,g-4)
    c: Coincident(g1,g2)
    c: Horizontal(g2)
    c: Distance(g1,g1) = 4
    c: Coincident(g1,g3)
    c: PointOnObject(g3,g-2)
    c: Coincident(g3,g4)
    c: Horizontal(g4)
    c: Coincident(g4,g5)
    c: PointOnObject(g5,g2)
    c: Vertical(g5)
    c: Coincident(g5,g6)
    c: PointOnObject(g6,g2)
    c: Coincident(g6,g7)
    c: Vertical(g7)
    c: Distance(g4,g4) = 3
    c: Equal(g3,g7)
    c: Distance(g3,g3) = 25
    c: Coincident(g7,g8)
    c: Horizontal(g8)
    c: Equal(g4,g8)
    c: DistanceX(g6,g6) = 88.6
    c: Coincident(g0,g9)
    c: Coincident(g9,g-7)
    c: Coincident(g9,g10)
    c: Coincident(g10,g8)
    c: PointOnObject(g8,g-7)
    c: Coincident(g0,g-6)
    c: PointOnObject(g2,g9)
FEATURE [PartDesign::Pad] Pad006
  BaseFeature = -> Pad005
  Direction = (0,-1,2e-16)
  Length = 57.5
  Length2 = 10
  Placement = pos=(0,0,0) rot=(1,0,0;1.5708rad)
  Profile = -> Sketch012
  ReferenceAxis = -> Sketch012 [N_Axis]
  Refine = true
  Suppressed = false
  Type = 0
FEATURE [Sketcher::SketchObject] Sketch013
  ArcFitTolerance = 1e-06
  AttachmentSupport = -> [Pad006]
  ExternalGeometry = -> [Pad006]
  FullyConstrained = true
  MakeInternals = false
  MapMode = 5
  Placement = pos=(0,-115.5,2.89e-14) rot=(1,0,0;1.5708rad)
  sketch-geometry (9):
    g0: LineSegment StartX=94.6 StartY=13 StartZ=0 EndX=94.6 EndY=29 EndZ=0
    g1: LineSegment StartX=94.6 StartY=29 StartZ=0 EndX=94.6 EndY=29 EndZ=0
    g2: LineSegment StartX=94.6 StartY=29 StartZ=0 EndX=0 EndY=29 EndZ=0
    g3: LineSegment StartX=0 StartY=29 StartZ=0 EndX=0 EndY=-3.6e-15 EndZ=0
    g4: Circle CenterX=15.1 CenterY=22.1 CenterZ=0 NormalX=0 NormalY=0 NormalZ=1 AngleXU=0 Radius=4.1
    g5: LineSegment [constr] StartX=11 StartY=22.1 StartZ=0 EndX=3 EndY=22.1 EndZ=0
    g6: LineSegment [constr] StartX=15.1 StartY=18 StartZ=0 EndX=15.1 EndY=4 EndZ=0
    g7: LineSegment StartX=0 StartY=-3.6e-15 StartZ=0 EndX=97.6 EndY=-3.6e-15 EndZ=0
    g8: LineSegment StartX=94.6 StartY=13 StartZ=0 EndX=97.6 EndY=-3.6e-15 EndZ=0
  constraints (23):
    c: Coincident(g0,g-6)
    c: Coincident(g0,g1)
    c: Coincident(g1,g-7)
    c: Coincident(g1,g2)
    c: Coincident(g2,g-8)
    c: Coincident(g2,g3)
    c: Diameter(g4) = 8.2
    c: PointOnObject(g5,g4)
    c: PointOnObject(g5,g-10)
    c: Horizontal(g5)
    c: PointOnObject(g6,g4)
    c: PointOnObject(g6,g-9)
    c: Vertical(g6)
    c: Perpendicular(g4,g6)
    c: Perpendicular(g4,g5)
    c: DistanceX(g5,g5) = 8
    c: DistanceY(g6,g6) = 14
    c: Coincident(g7,g3)
    c: Coincident(g7,g-5)
    c: Coincident(g8,g0)
    c: Coincident(g8,g7)
    c: Coincident(g-6,g0)
    c: Coincident(g3,g-1)
FEATURE [PartDesign::Pad] Pad007
  BaseFeature = -> Pad006
  Direction = (0,-1,2e-16)
  Length = 3
  Length2 = 10
  Placement = pos=(0,0,0) rot=(1,0,0;1.5708rad)
  Profile = -> Sketch013
  ReferenceAxis = -> Sketch013 [N_Axis]
  Refine = true
  Suppressed = false
  Type = 0
FEATURE [Sketcher::SketchObject] Sketch014
  ArcFitTolerance = 1e-06
  AttachmentSupport = -> [Pad007]
  ExternalGeometry = -> [Pad007]
  FullyConstrained = true
  MakeInternals = false
  MapMode = 5
  Placement = pos=(0,-55,1.65e-14) rot=(-1,0,0;1.5708rad)
  sketch-geometry (3):
    g0: LineSegment StartX=63.1208 StartY=-9 StartZ=0 EndX=51.1 EndY=-9 EndZ=0
    g1: LineSegment StartX=51.1 StartY=-9 StartZ=0 EndX=51.1 EndY=-21.0208 EndZ=0
    g2: LineSegment StartX=51.1 StartY=-21.0208 StartZ=0 EndX=63.1208 EndY=-9 EndZ=0
  constraints (8):
    c: PointOnObject(g0,g-3)
    c: Coincident(g0,g-4)
    c: Coincident(g0,g1)
    c: PointOnObject(g1,g-4)
    c: Coincident(g1,g2)
    c: Coincident(g2,g0)
    c: Equal(g1,g0)
    c: Distance(g0,g2) = 8.5
FEATURE [PartDesign::Pad] Pad008
  BaseFeature = -> Pad007
  Direction = (0,1,2e-16)
  Length = 10
  Length2 = 10
  Placement = pos=(0,0,0) rot=(1,0,0;1.5708rad)
  Profile = -> Sketch014
  ReferenceAxis = -> Sketch014 [N_Axis]
  Refine = true
  Suppressed = false
  Type = 3
  UpToFace = -> Pad007 [Face6]
FEATURE [PartDesign::Hole] Hole
  BaseFeature = -> Pad008
  CustomThreadClearance = 0
  Depth = 25
  DepthType = 0
  Diameter = 6.5
  DrillForDepth = false
  DrillPoint = 1
  DrillPointAngle = 118
  HoleCutCountersinkAngle = 90
  HoleCutCustomValues = false
  HoleCutDepth = 0
  HoleCutDiameter = 6.1
  HoleCutType = 0
  ModelThread = false
  Placement = pos=(0,0,0) rot=(1,0,0;1.5708rad)
  Profile = -> Pad008 [Face30,Face31]
  Refine = true
  Suppressed = false
  Tapered = false
  TaperedAngle = 90
  ThreadClass = 0
  ThreadDepth = 25
  ThreadDepthType = 0
  ThreadDirection = 0
  ThreadFit = 0
  ThreadSize = 0
  ThreadType = 0
  Threaded = false
  UseCustomThreadClearance = false
FEATURE [Sketcher::SketchObject] Sketch015
  ArcFitTolerance = 1e-06
  AttachmentSupport = -> [Hole]
  ExternalGeometry = -> [Hole]
  FullyConstrained = true
  MakeInternals = false
  MapMode = 5
  Placement = pos=(0,-58,1.45e-14) rot=(-1,0,0;1.5708rad)
  sketch-geometry (3):
    g0: LineSegment StartX=94.6 StartY=-13 StartZ=0 EndX=94.6 EndY=-29 EndZ=0
    g1: LineSegment StartX=94.6 StartY=-29 StartZ=0 EndX=94.6 EndY=-29 EndZ=0
    g2: LineSegment StartX=94.6 StartY=-29 StartZ=0 EndX=94.6 EndY=-13 EndZ=0
  constraints (7):
    c: Coincident(g-4,g0)
    c: Coincident(g0,g-6)
    c: Coincident(g0,g1)
    c: PointOnObject(g1,g-5)
    c: Coincident(g1,g2)
    c: Coincident(g2,g0)
    c: Horizontal(g1)
FEATURE [Sketcher::SketchObject] Sketch016
  ArcFitTolerance = 1e-06
  FullyConstrained = true
  MakeInternals = false
  MapMode = 5
  Placement = pos=(91.6,0,0) rot=(0.707107,0,-0.707107;3.14159rad)
  sketch-geometry (9):
    g0: ArcOfCircle CenterX=-17.75 CenterY=91 CenterZ=0 NormalX=0 NormalY=0 NormalZ=1 AngleXU=0 Radius=5.5 StartAngle=0 EndAngle=3.14159
    g1: ArcOfCircle CenterX=-17.75 CenterY=83 CenterZ=0 NormalX=0 NormalY=0 NormalZ=1 AngleXU=0 Radius=5.5 StartAngle=3.14159 EndAngle=6.28319
    g2: LineSegment StartX=-12.25 StartY=91 StartZ=0 EndX=-12.25 EndY=83 EndZ=0
    g3: LineSegment StartX=-23.25 StartY=91 StartZ=0 EndX=-23.25 EndY=83 EndZ=0
    g4: LineSegment [constr] StartX=-17.75 StartY=77.5 StartZ=0 EndX=-17.75 EndY=83 EndZ=0
    g5: LineSegment [constr] StartX=-17.75 StartY=83 StartZ=0 EndX=-17.75 EndY=91 EndZ=0
    g6: LineSegment [constr] StartX=-17.75 StartY=91 StartZ=0 EndX=-17.75 EndY=96.5 EndZ=0
    g7: LineSegment [constr] StartX=-17.75 StartY=77.5 StartZ=0 EndX=-17.75 EndY=58 EndZ=0
    g8: LineSegment [constr] StartX=-17.75 StartY=96.5 StartZ=0 EndX=-17.75 EndY=115.5 EndZ=0
  constraints (25):
    c: Tangent(g0,g2) = 1.5708
    c: Tangent(g0,g3) = -1.5708
    c: Tangent(g1,g2) = 1.5708
    c: Tangent(g1,g3) = -1.5708
    c: Equal(g0,g1)
    c: Vertical(g2)
    c: PointOnObject(g4,g1)
    c: Coincident(g4,g1)
    c: Coincident(g5,g1)
    c: Coincident(g5,g0)
    c: Coincident(g6,g0)
    c: PointOnObject(g6,g0)
    c: Vertical(g6)
    c: Vertical(g4)
    c: DistanceY(g4,g6) = 19
    c: DistanceX(g0,g0) = 11
    c: PointOnObject(g7,g-6)
    c: Vertical(g7)
    c: Coincident(g8,g6)
    c: PointOnObject(g8,g-3)
    c: Vertical(g8)
    c: Coincident(g7,g4)
    c: DistanceY(g8,g8) = 19
    c: DistanceY(g7,g7) = 19.5
    c: Distance(g1,g-4) = 13.75
FEATURE [PartDesign::Pocket] Pocket006
  BaseFeature = -> Hole
  Direction = (1,0,2e-16)
  Length = 5
  Length2 = 5
  Placement = pos=(0,0,0) rot=(1,0,0;1.5708rad)
  Profile = -> Sketch016
  ReferenceAxis = -> Sketch016 [N_Axis]
  Refine = true
  Suppressed = false
  Type = 1
FEATURE [Sketcher::SketchObject] Sketch017
  ArcFitTolerance = 1e-06
  AttachmentSupport = -> [Pocket006]
  ExternalGeometry = -> [Pocket006]
  FullyConstrained = true
  MakeInternals = false
  MapMode = 5
  Placement = pos=(0,-3e-16,0) rot=(-1,0,0;1.5708rad)
  sketch-geometry (3):
    g0: LineSegment StartX=42.1 StartY=-6 StartZ=0 EndX=35.0289 EndY=-6 EndZ=0
    g1: LineSegment StartX=35.0289 StartY=-6 StartZ=0 EndX=42.1 EndY=-13.0711 EndZ=0
    g2: LineSegment StartX=42.1 StartY=-13.0711 StartZ=0 EndX=42.1 EndY=-6 EndZ=0
  constraints (8):
    c: Coincident(g-4,g0)
    c: Horizontal(g0)
    c: Coincident(g0,g1)
    c: PointOnObject(g1,g-4)
    c: Coincident(g1,g2)
    c: Coincident(g2,g0)
    c: Equal(g0,g2)
    c: Distance(g0,g1) = 5
FEATURE [PartDesign::Pad] Pad010
  BaseFeature = -> Pocket006
  Direction = (0,1,2e-16)
  Length = 3.5
  Length2 = 10
  Placement = pos=(0,0,0) rot=(1,0,0;1.5708rad)
  Profile = -> Sketch017
  ReferenceAxis = -> Sketch017 [N_Axis]
  Refine = true
  Reversed = true
  Suppressed = false
  Type = 0
FEATURE [Sketcher::SketchObject] Sketch018
  ArcFitTolerance = 1e-06
  AttachmentSupport = -> [Pad010]
  ExternalGeometry = -> [Pad010]
  FullyConstrained = true
  MakeInternals = false
  MapMode = 5
  Placement = pos=(0,-58,1.74e-14) rot=(1,0,0;1.5708rad)
  sketch-geometry (3):
    g0: LineSegment StartX=35.0289 StartY=6 StartZ=0 EndX=42.1 EndY=6 EndZ=0
    g1: LineSegment StartX=42.1 StartY=6 StartZ=0 EndX=42.1 EndY=13.0711 EndZ=0
    g2: LineSegment StartX=42.1 StartY=13.0711 StartZ=0 EndX=35.0289 EndY=6 EndZ=0
  constraints (8):
    c: PointOnObject(g0,g-4)
    c: Coincident(g0,g-4)
    c: Coincident(g0,g1)
    c: PointOnObject(g1,g-3)
    c: Coincident(g1,g2)
    c: Coincident(g2,g0)
    c: Equal(g0,g1)
    c: Distance(g0,g2) = 5
FEATURE [PartDesign::Pad] Pad011
  BaseFeature = -> Pad010
  Direction = (0,-1,2e-16)
  Length = 3.5
  Length2 = 10
  Placement = pos=(0,0,0) rot=(1,0,0;1.5708rad)
  Profile = -> Sketch018
  ReferenceAxis = -> Sketch018 [N_Axis]
  Refine = true
  Reversed = true
  Suppressed = false
  Type = 0
FEATURE [Sketcher::SketchObject] Sketch019
  ArcFitTolerance = 1e-06
  AttachmentSupport = -> [Pad011]
  ExternalGeometry = -> [Pad011]
  FullyConstrained = true
  MakeInternals = false
  MapMode = 5
  Placement = pos=(0,-55,1.65e-14) rot=(-1,0,0;1.5708rad)
  sketch-geometry (24):
    g0: Circle [constr] CenterX=88.1 CenterY=-47.13 CenterZ=0 NormalX=0 NormalY=0 NormalZ=1 AngleXU=0 Radius=1.5
    g1: Circle [constr] CenterX=88.1 CenterY=-32.04 CenterZ=0 NormalX=0 NormalY=0 NormalZ=1 AngleXU=0 Radius=1.5
    g2: LineSegment [constr] StartX=88.1 StartY=-32.04 StartZ=0 EndX=88.1 EndY=-30.54 EndZ=0
    g3: LineSegment [constr] StartX=88.1 StartY=-30.54 StartZ=0 EndX=88.1 EndY=-13 EndZ=0
    g4: LineSegment [constr] StartX=88.1 StartY=-47.13 StartZ=0 EndX=88.1 EndY=-45.63 EndZ=0
    g5: LineSegment [constr] StartX=88.1 StartY=-45.63 StartZ=0 EndX=88.1 EndY=-33.54 EndZ=0
    g6: LineSegment [constr] StartX=88.1 StartY=-33.54 StartZ=0 EndX=88.1 EndY=-32.04 EndZ=0
    g7: LineSegment StartX=94.6 StartY=-44.88 StartZ=0 EndX=88.1 EndY=-44.88 EndZ=0
    g8: LineSegment StartX=88.1 StartY=-44.88 StartZ=0 EndX=85.85 EndY=-44.88 EndZ=0
    g9: LineSegment StartX=85.85 StartY=-44.88 StartZ=0 EndX=85.85 EndY=-49.55 EndZ=0
    g10: LineSegment [constr] StartX=88.1 StartY=-45.63 StartZ=0 EndX=88.1 EndY=-44.88 EndZ=0
    g11: LineSegment [constr] StartX=86.6 StartY=-47.13 StartZ=0 EndX=85.85 EndY=-47.13 EndZ=0
    g12: LineSegment StartX=85.85 StartY=-49.55 StartZ=0 EndX=94.6 EndY=-49.55 EndZ=0
    g13: LineSegment StartX=94.6 StartY=-44.88 StartZ=0 EndX=94.6 EndY=-49.55 EndZ=0
    g14: Circle CenterX=88.1 CenterY=-47.13 CenterZ=0 NormalX=0 NormalY=0 NormalZ=1 AngleXU=0 Radius=1.4
    g15: Circle CenterX=88.1 CenterY=-32.04 CenterZ=0 NormalX=0 NormalY=0 NormalZ=1 AngleXU=0 Radius=1.4
    g16: LineSegment StartX=94.6 StartY=-34.29 StartZ=0 EndX=85.85 EndY=-34.29 EndZ=0
    g17: LineSegment StartX=85.85 StartY=-34.29 StartZ=0 EndX=85.85 EndY=-28.54 EndZ=0
    g18: LineSegment StartX=85.85 StartY=-28.54 StartZ=0 EndX=94.6 EndY=-28.54 EndZ=0
    g19: LineSegment StartX=94.6 StartY=-34.29 StartZ=0 EndX=94.6 EndY=-28.54 EndZ=0
    g20: LineSegment [constr] StartX=88.1 StartY=-33.54 StartZ=0 EndX=88.1 EndY=-34.29 EndZ=0
    g21: LineSegment [constr] StartX=86.6 StartY=-32.04 StartZ=0 EndX=85.85 EndY=-32.04 EndZ=0
    g22: LineSegment [constr] StartX=88.1 StartY=-30.54 StartZ=0 EndX=88.1 EndY=-28.54 EndZ=0
    g23: LineSegment [constr] StartX=89.6 StartY=-32.04 StartZ=0 EndX=94.6 EndY=-32.04 EndZ=0
  constraints (72):
    c: Equal(g1,g0)
    c: DistanceX(g-3,g-3) = 13.3
    c: Coincident(g2,g1)
    c: PointOnObject(g2,g1)
    c: Vertical(g2)
    c: PointOnObject(g3,g-3)
    c: Vertical(g3)
    c: Coincident(g3,g2)
    c: Distance(g0,g-4) = 6.5
    c: DistanceY(g3,g3) = 17.54
    c: Coincident(g4,g0)
    c: PointOnObject(g4,g0)
    c: Vertical(g4)
    c: Coincident(g4,g5)
    c: PointOnObject(g5,g1)
    c: Vertical(g5)
    c: Coincident(g5,g6)
    c: Coincident(g6,g1)
    c: Vertical(g6)
    c: DistanceY(g5,g5) = 12.09
    c: Diameter(g0) = 3
    c: PointOnObject(g7,g5)
    c: Horizontal(g7)
    c: Coincident(g7,g8)
    c: Horizontal(g8)
    c: Coincident(g8,g9)
    c: Vertical(g9)
    c: Coincident(g10,g4)
    c: Coincident(g10,g7)
    c: PointOnObject(g11,g9)
    c: Horizontal(g11)
    c: PointOnObject(g11,g0)
    c: Perpendicular(g0,g11)
    c: Equal(g10,g11)
    c: PointOnObject(g9,g-5)
    c: PointOnObject(g7,g-4)
    c: Coincident(g12,g9)
    c: Coincident(g12,g-5)
    c: Coincident(g13,g7)
    c: Coincident(g13,g12)
    c: Coincident(g14,g0)
    c: Diameter(g14) = 2.8
    c: DistanceY(g10,g10) = 0.75
    c: Coincident(g15,g1)
    c: Equal(g15,g14)
    c: PointOnObject(g16,g-4)
    c: Horizontal(g16)
    c: Coincident(g16,g17)
    c: Vertical(g17)
    c: Coincident(g17,g18)
    c: PointOnObject(g18,g-4)
    c: Horizontal(g18)
    c: Coincident(g19,g16)
    c: Coincident(g19,g18)
    c: Coincident(g20,g6)
    c: PointOnObject(g20,g16)
    c: Vertical(g20)
    c: PointOnObject(g21,g1)
    c: PointOnObject(g21,g17)
    c: Horizontal(g21)
    c: Perpendicular(g1,g21)
    c: Equal(g20,g21)
    c: Equal(g20,g10)
    c: Coincident(g22,g2)
    c: PointOnObject(g22,g18)
    c: Vertical(g22)
    c: DistanceY(g22,g22) = 2
    c: PointOnObject(g23,g1)
    c: PointOnObject(g23,g19)
    c: Horizontal(g23)
    c: Perpendicular(g1,g23)
    c: DistanceX(g23,g23) = 5
FEATURE [PartDesign::Pad] Pad012
  BaseFeature = -> Pad011
  Direction = (0,1,2e-16)
  Length = 3.5
  Length2 = 10
  Placement = pos=(0,0,0) rot=(1,0,0;1.5708rad)
  Profile = -> Sketch019
  ReferenceAxis = -> Sketch019 [N_Axis]
  Refine = true
  Suppressed = false
  Type = 0
FEATURE [Sketcher::SketchObject] Sketch020
  ArcFitTolerance = 1e-06
  AttachmentSupport = -> [Pad012]
  ExternalGeometry = -> [Pad012]
  FullyConstrained = true
  MakeInternals = false
  MapMode = 5
  Placement = pos=(0,-55,1.65e-14) rot=(-1,0,0;1.5708rad)
  sketch-geometry (24):
    g0: ArcOfCircle CenterX=69.0132 CenterY=-37.0994 CenterZ=0 NormalX=0 NormalY=0 NormalZ=1 AngleXU=0 Radius=3.83685 StartAngle=1e-15 EndAngle=3.14159
    g1: ArcOfCircle CenterX=69.0132 CenterY=-42.0706 CenterZ=0 NormalX=0 NormalY=0 NormalZ=1 AngleXU=0 Radius=3.83685 StartAngle=3.14159 EndAngle=6.28319
    g2: LineSegment StartX=72.85 StartY=-37.0994 StartZ=0 EndX=72.85 EndY=-42.0706 EndZ=0
    g3: LineSegment StartX=65.1763 StartY=-37.0994 StartZ=0 EndX=65.1763 EndY=-42.0706 EndZ=0
    g4: LineSegment [constr] StartX=69.0132 StartY=-37.0994 StartZ=0 EndX=69.0132 EndY=-33.2625 EndZ=0
    g5: LineSegment [constr] StartX=69.0132 StartY=-37.0994 StartZ=0 EndX=69.0132 EndY=-42.0706 EndZ=0
    g6: LineSegment [constr] StartX=69.0132 StartY=-42.0706 StartZ=0 EndX=69.0132 EndY=-45.9075 EndZ=0
    g7: LineSegment [constr] StartX=71.8382 StartY=-43.2 StartZ=0 EndX=71.8382 EndY=-35.97 EndZ=0
    g8: LineSegment [constr] StartX=71.8382 StartY=-35.97 StartZ=0 EndX=66.1882 EndY=-35.97 EndZ=0
    g9: LineSegment [constr] StartX=66.1882 StartY=-35.97 StartZ=0 EndX=66.1882 EndY=-43.2 EndZ=0
    g10: LineSegment [constr] StartX=66.1882 StartY=-43.2 StartZ=0 EndX=71.8382 EndY=-43.2 EndZ=0
    g11: LineSegment [constr] StartX=72.4382 StartY=-43.8 StartZ=0 EndX=72.4382 EndY=-35.37 EndZ=0
    g12: LineSegment [constr] StartX=72.4382 StartY=-35.37 StartZ=0 EndX=65.5882 EndY=-35.37 EndZ=0
    g13: LineSegment [constr] StartX=65.5882 StartY=-35.37 StartZ=0 EndX=65.5882 EndY=-43.8 EndZ=0
    g14: LineSegment [constr] StartX=65.5882 StartY=-43.8 StartZ=0 EndX=72.4382 EndY=-43.8 EndZ=0
    g15: LineSegment [constr] StartX=71.8382 StartY=-43.2 StartZ=0 EndX=72.4382 EndY=-43.8 EndZ=0
    g16: LineSegment [constr] StartX=71.8382 StartY=-35.97 StartZ=0 EndX=72.4382 EndY=-35.37 EndZ=0
    g17: LineSegment [constr] StartX=66.1882 StartY=-35.97 StartZ=0 EndX=65.5882 EndY=-35.37 EndZ=0
    g18: LineSegment [constr] StartX=66.1882 StartY=-43.2 StartZ=0 EndX=65.5882 EndY=-43.8 EndZ=0
    g19: LineSegment [constr] StartX=66.1882 StartY=-43.2 StartZ=0 EndX=65.5882 EndY=-43.2 EndZ=0
    g20: Circle CenterX=88.1 CenterY=-47.13 CenterZ=0 NormalX=0 NormalY=0 NormalZ=1 AngleXU=0 Radius=1.4
    g21: Circle CenterX=88.1 CenterY=-32.04 CenterZ=0 NormalX=0 NormalY=0 NormalZ=1 AngleXU=0 Radius=1.4
    g22: LineSegment [constr] StartX=85.85 StartY=-44.88 StartZ=0 EndX=85.85 EndY=-34.29 EndZ=0
    g23: LineSegment [constr] StartX=85.85 StartY=-39.585 StartZ=0 EndX=72.85 EndY=-39.585 EndZ=0
  constraints (62):
    c: Tangent(g0,g2) = 1.5708
    c: Tangent(g0,g3) = -1.5708
    c: Tangent(g1,g2) = 1.5708
    c: Tangent(g1,g3) = -1.5708
    c: Equal(g0,g1)
    c: Vertical(g2)
    c: Coincident(g4,g0)
    c: PointOnObject(g4,g0)
    c: Vertical(g4)
    c: Coincident(g5,g0)
    c: Coincident(g5,g1)
    c: Coincident(g6,g1)
    c: PointOnObject(g6,g1)
    c: Vertical(g6)
    c: Coincident(g7,g8)
    c: Coincident(g8,g9)
    c: Coincident(g9,g10)
    c: Coincident(g10,g7)
    c: Vertical(g7)
    c: Vertical(g9)
    c: Horizontal(g8)
    c: Horizontal(g10)
    c: Coincident(g11,g12)
    c: Coincident(g12,g13)
    c: Coincident(g13,g14)
    c: Coincident(g14,g11)
    c: Vertical(g11)
    c: Vertical(g13)
    c: Horizontal(g12)
    c: Horizontal(g14)
    c: Coincident(g15,g7)
    c: Coincident(g15,g11)
    c: Coincident(g16,g8)
    c: Coincident(g16,g12)
    c: Coincident(g17,g9)
    c: Coincident(g17,g13)
    c: Coincident(g18,g10)
    c: Coincident(g18,g14)
    c: Perpendicular(g15,g16)
    c: Perpendicular(g16,g17)
    c: Perpendicular(g17,g18)
    c: Coincident(g19,g9)
    c: PointOnObject(g19,g13)
    c: Horizontal(g19)
    c: DistanceX(g19,g19) = 0.6
    c: PointOnObject(g11,g1)
    c: PointOnObject(g13,g1)
    c: PointOnObject(g12,g0)
    c: DistanceX(g10,g10) = 5.65
    c: DistanceY(g7,g7) = 7.23
    c: DistanceY(g3,g3) = 4.97124
    c: Radius(g0) = 3.83685
    c: Coincident(g20,g-9)
    c: Equal(g20,g-9)
    c: Coincident(g21,g-10)
    c: Equal(g21,g-10)
    c: Coincident(g22,g-8)
    c: Coincident(g22,g-6)
    c: Symmetric(g22,g22,g23)
    c: Symmetric(g2,g2,g23)
    c: Horizontal(g23)
    c: DistanceX(g23,g23) = 13
FEATURE [PartDesign::Pocket] Pocket007
  BaseFeature = -> Pad012
  Direction = (0,-1,-2e-16)
  Length = 5
  Length2 = 5
  Placement = pos=(0,0,0) rot=(1,0,0;1.5708rad)
  Profile = -> Sketch020
  ReferenceAxis = -> Sketch020 [N_Axis]
  Refine = true
  Suppressed = false
  Type = 0
FEATURE [Sketcher::SketchObject] Sketch021
  ArcFitTolerance = 1e-06
  AttachmentSupport = -> [Pad012]
  ExternalGeometry = -> [Pad012]
  FullyConstrained = true
  MakeInternals = false
  MapMode = 5
  Placement = pos=(0,-55,1.65e-14) rot=(-1,0,0;1.5708rad)
  sketch-geometry (6):
    g0: LineSegment StartX=94.6 StartY=-34.29 StartZ=0 EndX=94.6 EndY=-44.88 EndZ=0
    g1: LineSegment StartX=94.6 StartY=-44.88 StartZ=0 EndX=85.85 EndY=-44.88 EndZ=0
    g2: LineSegment StartX=85.85 StartY=-44.88 StartZ=0 EndX=76.85 EndY=-44.88 EndZ=0
    g3: LineSegment StartX=76.85 StartY=-44.88 StartZ=0 EndX=76.85 EndY=-34.29 EndZ=0
    g4: LineSegment StartX=76.85 StartY=-34.29 StartZ=0 EndX=85.85 EndY=-34.29 EndZ=0
    g5: LineSegment StartX=85.85 StartY=-34.29 StartZ=0 EndX=94.6 EndY=-34.29 EndZ=0
  constraints (14):
    c: Coincident(g-5,g0)
    c: Coincident(g0,g-5)
    c: Coincident(g0,g1)
    c: Coincident(g1,g-4)
    c: Coincident(g1,g2)
    c: Horizontal(g2)
    c: Coincident(g2,g3)
    c: Vertical(g3)
    c: Coincident(g3,g4)
    c: Coincident(g4,g-3)
    c: Horizontal(g4)
    c: Coincident(g4,g5)
    c: Coincident(g5,g0)
    c: DistanceX(g4,g4) = 9
FEATURE [PartDesign::Pocket] Pocket008
  BaseFeature = -> Pocket007
  Direction = (0,-1,-2e-16)
  Length = 5
  Length2 = 5
  Placement = pos=(0,0,0) rot=(1,0,0;1.5708rad)
  Profile = -> Sketch021
  ReferenceAxis = -> Sketch021 [N_Axis]
  Refine = true
  Suppressed = false
  Type = 0
FEATURE [PartDesign::Body] Body001  label="Motor_Mount"
  AllowCompound = false
  Group = -> [Sketch002,Pad001,Sketch003,Pocket001,Sketch004,Pocket002,Sketch005,Pocket003,Chamfer,Sketch006,Pocket004,Chamfer001,Sketch011,Pad005,Sketch012,Pad006,Sketch013,Pad007,Sketch014,Pad008,Hole,Sketch015,Sketch016,Pocket006,Sketch017,Pad010,Sketch018,Pad011,Sketch019,Pad012,Sketch020,Pocket007,Sketch021,Pocket008]
  Origin = -> Origin001
  Placement = pos=(-26,-25,130) rot=(-0.57735,0.57735,0.57735;2.0944rad)
  Tip = -> Pocket008
FEATURE [App::Link] Motor_Mount  label="Motor_Mount001"
  LinkPlacement = pos=(-30.4,139.717,-54.0188) rot=(0,0,1;0rad)
  LinkedObject = -> Body001
  Placement = pos=(-30.4,139.717,-54.0188) rot=(0,0,1;0rad)
FEATURE [App::FeaturePython] GroundedJoint  # Assembly grounded joint (typed FeaturePython)
  ObjectToGround = -> Motor_Mount
  Placement = pos=(-30.4,139.717,-54.0188) rot=(0,0,1;0rad)
FEATURE [App::Link] Single_Block  label="Single_Block001"
  LinkPlacement = pos=(247.9,139.717,-54.0188) rot=(0,0,1;0rad)
  LinkedObject = -> Body
  Placement = pos=(247.9,139.717,-54.0188) rot=(0,0,1;0rad)
FEATURE [App::Link] Window_Grab_Clamp  label="Window_Grab_Clamp001"
  LinkPlacement = pos=(220.481,119.533,33.8312) rot=(-0.57735,0.57735,0.57735;4.18879rad)
  LinkedObject = -> Body003
  Placement = pos=(220.481,119.533,33.8312) rot=(-0.57735,0.57735,0.57735;4.18879rad)
FEATURE [App::Link] Window_Grab_Arm  label="Window_Grab_Arm001"
  LinkPlacement = pos=(235.407,92.2168,-25.5188) rot=(-0.57735,0.57735,0.57735;4.18879rad)
  LinkedObject = -> Body002
  Placement = pos=(235.407,92.2168,-25.5188) rot=(-0.57735,0.57735,0.57735;4.18879rad)
FEATURE [App::Link] Window_Grab_Arm_Clamp  label="Window_Grab_Arm_Clamp001"
  LinkPlacement = pos=(226.407,112.217,-25.5188) rot=(0,1,0;4.71239rad)
  LinkedObject = -> Body004
  Placement = pos=(226.407,112.217,-25.5188) rot=(0,1,0;4.71239rad)
FEATURE [App::FeaturePython] Joint  label="Parallel"  # Assembly joint (typed FeaturePython)
  Activated = true
  AngleMax = 0
  AngleMin = 0
  Detach1 = false
  Detach2 = false
  Distance = 0
  Distance2 = 0
  EnableAngleMax = false
  EnableAngleMin = false
  EnableLengthMax = false
  EnableLengthMin = false
  JointType = 6 (Parallel)
  LengthMax = 0
  LengthMin = 0
  Placement1 = pos=(51.1,-27.5,36.3401) rot=(0,-1,0;1.5708rad)
  Placement2 = pos=(-6.3,0,5) rot=(0,0,1;0rad)
  Reference1 = -> Assembly [Motor_Mount.Face48,Motor_Mount.Face48]
  Reference2 = -> Assembly [Window_Grab_Arm_Clamp.Face4,Window_Grab_Arm_Clamp.Vertex11]
FEATURE [App::FeaturePython] Joint001  label="Slider"  # Assembly joint (typed FeaturePython)
  Activated = true
  AngleMax = 0
  AngleMin = 0
  Detach1 = false
  Detach2 = false
  Distance = 0
  Distance2 = 0
  EnableAngleMax = false
  EnableAngleMin = false
  EnableLengthMax = true
  EnableLengthMin = true
  JointType = 3 (Slider)
  LengthMax = -55
  LengthMin = -220
  Placement1 = pos=(46.6,-27.5,28.5) rot=(0.707107,0,-0.707107;3.14159rad)
  Placement2 = pos=(0,0,2.5) rot=(0,0,1;0rad)
  Reference1 = -> Assembly [Motor_Mount.Face60,Motor_Mount.Face60]
  Reference2 = -> Assembly [Window_Grab_Arm_Clamp.Face5,Window_Grab_Arm_Clamp.Face5]
FEATURE [App::FeaturePython] Joint002  label="Parallel001"  # Assembly joint (typed FeaturePython)
  Activated = true
  AngleMax = 0
  AngleMin = 0
  Detach1 = false
  Detach2 = false
  Distance = 0
  Distance2 = 0
  EnableAngleMax = false
  EnableAngleMin = false
  EnableLengthMax = false
  EnableLengthMin = false
  JointType = 6 (Parallel)
  LengthMax = 0
  LengthMin = 0
  Offset1 = pos=(0,0,200) rot=(0,0,1;0rad)
  Placement1 = pos=(297.6,0,0) rot=(0.707107,0,0.707107;3.14159rad)
  Placement2 = pos=(19.3,0,0) rot=(0.707107,0,0.707107;3.14159rad)
  Reference1 = -> Assembly [Motor_Mount.Edge115,Motor_Mount.Vertex87]
  Reference2 = -> Assembly [Single_Block.Edge40,Single_Block.Vertex34]
FEATURE [App::FeaturePython] Joint005  label="Slider002"  # Assembly joint (typed FeaturePython)
  Activated = true
  AngleMax = 0
  AngleMin = 0
  Detach1 = false
  Detach2 = false
  Distance = 0
  Distance2 = 0
  EnableAngleMax = false
  EnableAngleMin = false
  EnableLengthMax = true
  EnableLengthMin = true
  JointType = 3 (Slider)
  LengthMax = 20
  LengthMin = 0
  Offset1 = pos=(0,0,0) rot=(1,0,0;1.5708rad)
  Offset2 = pos=(0,0,1) rot=(0.57735,0.57735,0.57735;2.0944rad)
  Placement1 = pos=(5.25,0,0) rot=(1,0,0;1.5708rad)
  Placement2 = pos=(0,5.25,9) rot=(0.57735,0.57735,0.57735;2.0944rad)
  Reference1 = -> Assembly [Window_Grab_Arm_Clamp.Vertex4,Window_Grab_Arm_Clamp.Vertex4]
  Reference2 = -> Assembly [Window_Grab_Arm.Vertex37,Window_Grab_Arm.Vertex37]
FEATURE [App::FeaturePython] Joint006  label="Slider003"  # Assembly joint (typed FeaturePython)
  Activated = true
  AngleMax = 0
  AngleMin = 0
  Detach1 = false
  Detach2 = false
  Distance = 0
  Distance2 = 0
  EnableAngleMax = false
  EnableAngleMin = false
  EnableLengthMax = true
  EnableLengthMin = true
  JointType = 3 (Slider)
  LengthMax = 20
  LengthMin = 0
  Placement1 = pos=(-35.691,50.975,8) rot=(0,0,1;0rad)
  Placement2 = pos=(-8.375,-8.375,0) rot=(0,0,1;0rad)
  Reference1 = -> Assembly [Window_Grab_Arm.Edge56,Window_Grab_Arm.Edge56]
  Reference2 = -> Assembly [Window_Grab_Clamp.Edge16,Window_Grab_Clamp.Edge16]
FEATURE [Assembly::JointGroup] Joints
  Group = -> [GroundedJoint,Joint,Joint001,Joint002,Joint005,Joint006]
FEATURE [Assembly::AssemblyObject] Assembly
  Group = -> [Joints,Motor_Mount,GroundedJoint,Single_Block,Window_Grab_Clamp,Window_Grab_Arm,Window_Grab_Arm_Clamp,Joint,Joint001,Joint002,Joint005,Joint006]
  Origin = -> Origin005
  Type = Assembly
FEATURE [Sketcher::SketchObject] Sketch022
  ArcFitTolerance = 1e-06
  AttachmentSupport = -> [Pocket]
  ExternalGeometry = -> [Pocket]
  FullyConstrained = true
  MakeInternals = false
  MapMode = 5
  Placement = pos=(0,-55,1.21e-14) rot=(1,0,0;1.5708rad)
  sketch-geometry (34):
    g0: LineSegment StartX=16.3 StartY=13 StartZ=0 EndX=19.3 EndY=0 EndZ=0
    g1: LineSegment StartX=19.3 StartY=0 StartZ=0 EndX=0 EndY=0 EndZ=0
    g2: LineSegment StartX=0 StartY=0 StartZ=0 EndX=-3 EndY=13 EndZ=0
    g3: LineSegment StartX=-3 StartY=13 StartZ=0 EndX=-3 EndY=47.3 EndZ=0
    g4: LineSegment StartX=-3 StartY=47.3 StartZ=0 EndX=16.3 EndY=47.3 EndZ=0
    g5: LineSegment StartX=16.3 StartY=13 StartZ=0 EndX=16.3 EndY=18.3 EndZ=0
    g6: LineSegment StartX=16.3 StartY=18.3 StartZ=0 EndX=16.3 EndY=24.3 EndZ=0
    g7: LineSegment StartX=16.3 StartY=47.3 StartZ=0 EndX=16.3 EndY=44.3 EndZ=0
    g8: LineSegment StartX=16.3 StartY=44.3 StartZ=0 EndX=16.3 EndY=24.3 EndZ=0
    g9: ArcOfCircle [constr] CenterX=2.05 CenterY=41.75 CenterZ=0 NormalX=0 NormalY=0 NormalZ=1 AngleXU=0 Radius=1.5 StartAngle=1.5708 EndAngle=4.71239
    g10: ArcOfCircle [constr] CenterX=11.25 CenterY=41.75 CenterZ=0 NormalX=0 NormalY=0 NormalZ=1 AngleXU=0 Radius=1.5 StartAngle=4.71239 EndAngle=7.85398
    g11: LineSegment [constr] StartX=2.05 StartY=43.25 StartZ=0 EndX=11.25 EndY=43.25 EndZ=0
    g12: LineSegment [constr] StartX=2.05 StartY=40.25 StartZ=0 EndX=11.25 EndY=40.25 EndZ=0
    g13: ArcOfCircle [constr] CenterX=2.05 CenterY=26.85 CenterZ=0 NormalX=0 NormalY=0 NormalZ=1 AngleXU=0 Radius=1.5 StartAngle=1.5708 EndAngle=4.71239
    g14: ArcOfCircle [constr] CenterX=11.25 CenterY=26.85 CenterZ=0 NormalX=0 NormalY=0 NormalZ=1 AngleXU=0 Radius=1.5 StartAngle=4.71239 EndAngle=7.85398
    g15: LineSegment [constr] StartX=2.05 StartY=28.35 StartZ=0 EndX=11.25 EndY=28.35 EndZ=0
    g16: LineSegment [constr] StartX=2.05 StartY=25.35 StartZ=0 EndX=11.25 EndY=25.35 EndZ=0
    g17: LineSegment [constr] StartX=2.05 StartY=41.75 StartZ=0 EndX=2.05 EndY=26.85 EndZ=0
    g18: LineSegment [constr] StartX=11.25 StartY=41.75 StartZ=0 EndX=11.25 EndY=26.85 EndZ=0
    g19: LineSegment [constr] StartX=16.3 StartY=24.3 StartZ=0 EndX=-3 EndY=24.3 EndZ=0
    g20: LineSegment [constr] StartX=16.3 StartY=44.3 StartZ=0 EndX=-3 EndY=44.3 EndZ=0
    g21: LineSegment [constr] StartX=6.65 StartY=24.3 StartZ=0 EndX=6.65 EndY=25.35 EndZ=0
    g22: LineSegment [constr] StartX=6.65 StartY=43.25 StartZ=0 EndX=6.65 EndY=44.3 EndZ=0
    g23: ArcOfCircle CenterX=2.05 CenterY=41.75 CenterZ=0 NormalX=0 NormalY=0 NormalZ=1 AngleXU=0 Radius=2.25 StartAngle=1.5708 EndAngle=4.71239
    g24: ArcOfCircle CenterX=11.25 CenterY=41.75 CenterZ=0 NormalX=0 NormalY=0 NormalZ=1 AngleXU=0 Radius=2.25 StartAngle=4.71239 EndAngle=7.85398
    g25: LineSegment StartX=2.05 StartY=44 StartZ=0 EndX=11.25 EndY=44 EndZ=0
    g26: LineSegment StartX=2.05 StartY=39.5 StartZ=0 EndX=11.25 EndY=39.5 EndZ=0
    g27: ArcOfCircle CenterX=2.05 CenterY=26.85 CenterZ=0 NormalX=0 NormalY=0 NormalZ=1 AngleXU=0 Radius=2.25 StartAngle=1.5708 EndAngle=4.71239
    g28: ArcOfCircle CenterX=11.25 CenterY=26.85 CenterZ=0 NormalX=0 NormalY=0 NormalZ=1 AngleXU=0 Radius=2.25 StartAngle=4.71239 EndAngle=7.85398
    g29: LineSegment StartX=2.05 StartY=29.1 StartZ=0 EndX=11.25 EndY=29.1 EndZ=0
    g30: LineSegment StartX=2.05 StartY=24.6 StartZ=0 EndX=11.25 EndY=24.6 EndZ=0
    g31: LineSegment [constr] StartX=-0.2 StartY=41.75 StartZ=0 EndX=-3 EndY=41.75 EndZ=0
    g32: LineSegment [constr] StartX=-3 StartY=13 StartZ=0 EndX=0 EndY=13 EndZ=0
    g33: LineSegment [constr] StartX=0 StartY=13 StartZ=0 EndX=3 EndY=13 EndZ=0
  constraints (84):
    c: Coincident(g0,g-6)
    c: Coincident(g1,g-6)
    c: Coincident(g1,g-5)
    c: Coincident(g2,g-5)
    c: Vertical(g3)
    c: Coincident(g4,g3)
    c: Horizontal(g4)
    c: Coincident(g0,g-4)
    c: Coincident(g5,g0)
    c: Vertical(g5)
    c: Coincident(g6,g5)
    c: Vertical(g6)
    c: Coincident(g7,g4)
    c: Vertical(g7)
    c: Coincident(g8,g7)
    c: Coincident(g8,g6)
    c: Vertical(g8)
    c: DistanceY(g5,g5) = 5.3
    c: DistanceY(g8,g8) = 20
    c: DistanceY(g7,g7) = 3
    c: DistanceY(g6,g6) = 6
    c: Tangent(g9,g11) = 1.5708
    c: Tangent(g9,g12) = -1.5708
    c: Tangent(g10,g11) = 1.5708
    c: Tangent(g10,g12) = -1.5708
    c: Equal(g9,g10)
    c: Radius(g9) = 1.5
    c: Horizontal(g11)
    c: Tangent(g13,g15) = 1.5708
    c: Tangent(g13,g16) = -1.5708
    c: Tangent(g14,g15) = 1.5708
    c: Tangent(g14,g16) = -1.5708
    c: Equal(g13,g14)
    c: Horizontal(g15)
    c: Equal(g14,g10)
    c: Coincident(g17,g9)
    c: Coincident(g17,g13)
    c: Vertical(g17)
    c: Coincident(g18,g10)
    c: Coincident(g18,g14)
    c: Vertical(g18)
    c: Coincident(g19,g6)
    c: PointOnObject(g19,g3)
    c: Horizontal(g19)
    c: Coincident(g20,g7)
    c: PointOnObject(g20,g3)
    c: Horizontal(g20)
    c: Symmetric(g19,g19,g21)
    c: Symmetric(g16,g16,g21)
    c: Vertical(g21)
    c: Symmetric(g11,g11,g22)
    c: Symmetric(g20,g20,g22)
    c: Equal(g22,g21)
    c: DistanceY(g22,g22) = 1.05
    c: Tangent(g23,g25) = 1.5708
    c: Tangent(g23,g26) = -1.5708
    c: Tangent(g24,g25) = 1.5708
    c: Tangent(g24,g26) = -1.5708
    c: Equal(g23,g24)
    c: Coincident(g23,g9)
    c: Coincident(g24,g10)
    c: Tangent(g27,g29) = 1.5708
    c: Tangent(g27,g30) = -1.5708
    c: Tangent(g28,g29) = 1.5708
    c: Tangent(g28,g30) = -1.5708
    c: Equal(g27,g28)
    c: Distance(g26,g12) = 0.75
    c: Equal(g24,g28)
    c: Coincident(g27,g13)
    c: Coincident(g28,g14)
    c: PointOnObject(g31,g23)
    c: PointOnObject(g31,g3)
    c: Horizontal(g31)
    c: Perpendicular(g23,g31)
    c: Distance(g31,g31) = 2.8
    c: Coincident(g2,g3)
    c: DistanceX(g16,g16) = 9.2
    c: Coincident(g2,g32)
    c: Horizontal(g32)
    c: Coincident(g32,g33)
    c: Coincident(g33,g-5)
    c: Horizontal(g33)
    c: Equal(g33,g32)
    c: PointOnObject(g32,g-2)
FEATURE [PartDesign::Pad] Pad013
  BaseFeature = -> Pocket
  Direction = (0,-1,2e-16)
  Length = 5
  Length2 = 10
  Placement = pos=(0,0,0) rot=(1,0,0;1.5708rad)
  Profile = -> Sketch022
  ReferenceAxis = -> Sketch022 [N_Axis]
  Refine = true
  Suppressed = false
  Type = 0
FEATURE [Sketcher::SketchObject] Sketch023
  ArcFitTolerance = 1e-06
  AttachmentSupport = -> [Pad013]
  ExternalGeometry = -> [Pad013]
  FullyConstrained = true
  MakeInternals = false
  MapMode = 5
  Placement = pos=(0,-55,0) rot=(-1,0,0;1.5708rad)
  sketch-geometry (14):
    g0: LineSegment StartX=10.25 StartY=-30.55 StartZ=0 EndX=10.25 EndY=-38.05 EndZ=0
    g1: LineSegment StartX=10.25 StartY=-38.05 StartZ=0 EndX=3.05 EndY=-38.05 EndZ=0
    g2: LineSegment StartX=3.05 StartY=-38.05 StartZ=0 EndX=3.05 EndY=-39.3 EndZ=0
    g3: LineSegment StartX=3.05 StartY=-39.3 StartZ=0 EndX=-3 EndY=-39.3 EndZ=0
    g4: LineSegment StartX=-3 StartY=-39.3 StartZ=0 EndX=-3 EndY=-31.05 EndZ=0
    g5: LineSegment StartX=-3 StartY=-31.05 StartZ=0 EndX=0.85 EndY=-31.05 EndZ=0
    g6: LineSegment StartX=0.85 StartY=-31.05 StartZ=0 EndX=0.85 EndY=-30.55 EndZ=0
    g7: LineSegment StartX=0.85 StartY=-30.55 StartZ=0 EndX=10.25 EndY=-30.55 EndZ=0
    g8: LineSegment StartX=4.25 StartY=-29.1 StartZ=0 EndX=-3 EndY=-29.1 EndZ=0
    g9: LineSegment StartX=-3 StartY=-29.1 StartZ=0 EndX=-3 EndY=-25.75 EndZ=0
    g10: LineSegment StartX=-3 StartY=-25.75 StartZ=0 EndX=4.25 EndY=-25.75 EndZ=0
    g11: LineSegment StartX=4.25 StartY=-25.75 StartZ=0 EndX=4.25 EndY=-29.1 EndZ=0
    g12: LineSegment [constr] StartX=13.5 StartY=-26.85 StartZ=0 EndX=13.5 EndY=-29.1 EndZ=0
    g13: LineSegment [constr] StartX=13.5 StartY=-29.1 StartZ=0 EndX=4.25 EndY=-29.1 EndZ=0
  constraints (41):
    c: Vertical(g0)
    c: Coincident(g0,g1)
    c: Horizontal(g1)
    c: Coincident(g1,g2)
    c: Vertical(g2)
    c: Coincident(g2,g3)
    c: Horizontal(g3)
    c: Coincident(g3,g4)
    c: Vertical(g4)
    c: Coincident(g4,g5)
    c: Horizontal(g5)
    c: Coincident(g5,g6)
    c: Vertical(g6)
    c: Coincident(g6,g7)
    c: Coincident(g7,g0)
    c: Horizontal(g7)
    c: Horizontal(g8)
    c: Coincident(g8,g9)
    c: Vertical(g9)
    c: Coincident(g9,g10)
    c: Horizontal(g10)
    c: Coincident(g10,g11)
    c: Coincident(g11,g8)
    c: Vertical(g11)
    c: Vertical(g12)
    c: Tangent(g12,g-8) = 1.5708
    c: Coincident(g13,g12)
    c: Coincident(g13,g8)
    c: Horizontal(g13)
    c: DistanceX(g13,g13) = 9.25
    c: PointOnObject(g8,g-10)
    c: DistanceY(g9,g9) = 3.35
    c: DistanceY(g0,g0) = 7.5
    c: DistanceY(g2,g2) = 1.25
    c: DistanceY(g12,g12) = 2.25
    c: Distance(g-12,g1) = 3.7
    c: DistanceX(g1,g1) = 7.2
    c: DistanceX(g0,g-12) = 1
    c: DistanceX(g6,g-9) = 1.2
    c: DistanceY(g4,g4) = 8.25
    c: PointOnObject(g3,g-10)
FEATURE [PartDesign::Pocket] Pocket009
  BaseFeature = -> Pad013
  Direction = (0,-1,-2e-16)
  Length = 2.5
  Length2 = 5
  Placement = pos=(0,0,0) rot=(1,0,0;1.5708rad)
  Profile = -> Sketch023
  ReferenceAxis = -> Sketch023 [N_Axis]
  Refine = true
  Suppressed = false
  Type = 0
FEATURE [PartDesign::Chamfer] Chamfer005
  Angle = 45
  Base = -> Pocket009 [Edge57,Edge45,Edge17,Edge56,Edge44,Edge46,Edge43,Edge40,Edge34]
  BaseFeature = -> Pocket009
  ChamferType = 0
  FlipDirection = false
  Placement = pos=(0,0,0) rot=(1,0,0;1.5708rad)
  Refine = true
  Size = 1
  Size2 = 1
  SupportTransform = false
  Suppressed = false
  UseAllEdges = false
FEATURE [PartDesign::Body] Body  label="Single_Block"
  AllowCompound = false
  Group = -> [Sketch,Pad,Sketch001,Pocket,Sketch022,Pad013,Sketch023,Pocket009,Chamfer005]
  Origin = -> Origin
  Placement = pos=(-26,-25,-23) rot=(-0.57735,0.57735,0.57735;2.0944rad)
  Tip = -> Chamfer005
